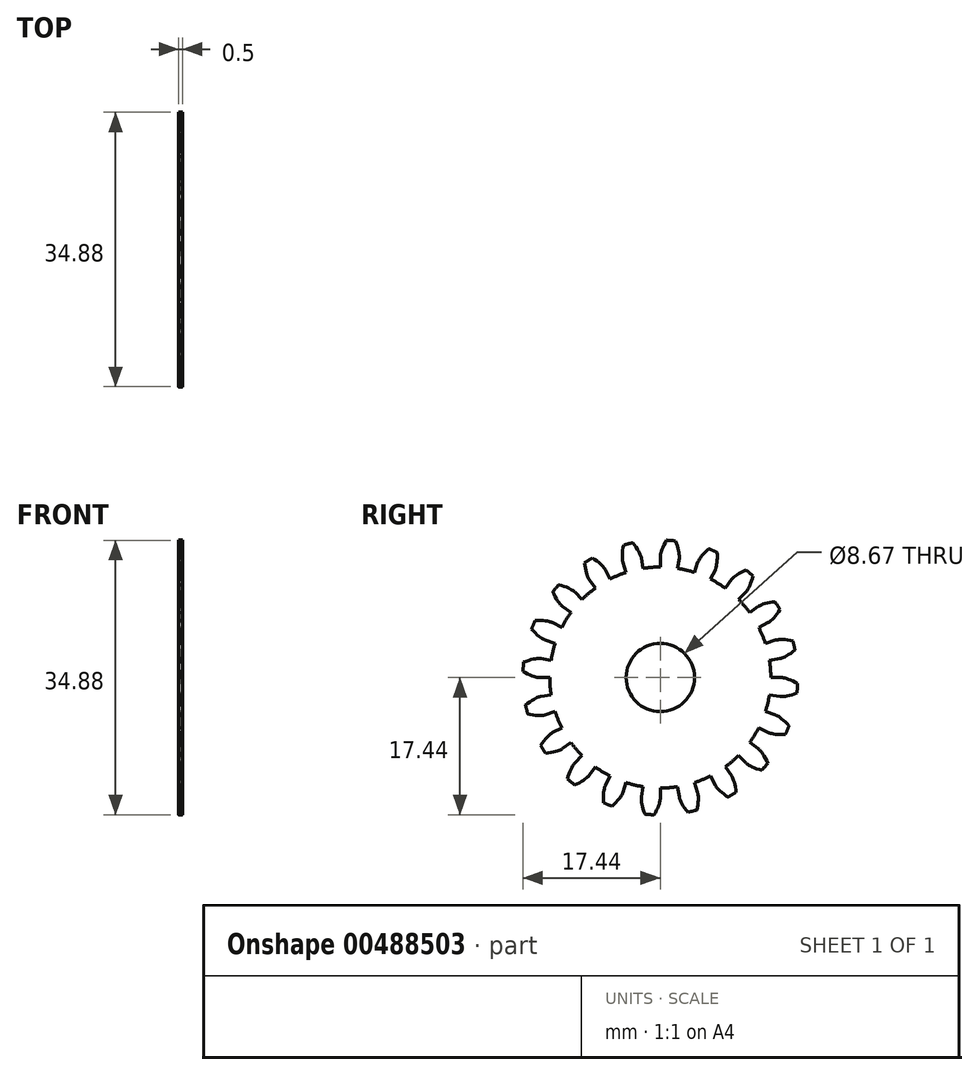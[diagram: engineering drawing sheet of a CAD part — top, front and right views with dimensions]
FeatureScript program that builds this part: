
annotation { "Feature Type Name" : "Feature", "Feature Type Description" : "" }
export const myFeature = defineFeature(function(context is Context, id is Id, definition is map)
    precondition{}
    {
        {
            assignVariable(context, id + "F0", {"name" : "GearThickness", "anyValue" : .5});
        }
        {
            var Q0;
            Q0=qCreatedBy(makeId("Right.planeOp"),FACE);
            var sketch = newSketch(context, id + "F1", { "sketchPlane" : qUnion([Q0])});
            skCircle(sketch, "E0", {"center": v(0, 0) * mm, "radius": 14.04 * mm});
            skCircle(sketch, "E1", {"center": v(0, 0) * mm, "radius": 15.37 * mm, "construction": true});
            skCircle(sketch, "E2", {"center": v(0, 0) * mm, "radius": 15.88 * mm, "construction": true});
            skCircle(sketch, "E3", {"center": v(0, 0) * mm, "radius": 17.46 * mm});
            skLineSegment(sketch, "E4", {"start": v(0, 0) * mm, "end": v(-15.37, 0) * mm, "construction": true});
            skLineSegment(sketch, "E5.1.0", {"start": v(0, 0) * mm, "end": v(-15.35, 0.77) * mm, "construction": true});
            skLineSegment(sketch, "E5.2.0", {"start": v(0, 0) * mm, "end": v(-15.3, 1.53) * mm, "construction": true});
            skLineSegment(sketch, "E5.3.0", {"start": v(0, 0) * mm, "end": v(-15.2, 2.3) * mm, "construction": true});
            skLineSegment(sketch, "E5.4.0", {"start": v(0, 0) * mm, "end": v(-15.06, 3.05) * mm, "construction": true});
            skLineSegment(sketch, "E5.5.0", {"start": v(0, 0) * mm, "end": v(-14.9, 3.8) * mm, "construction": true});
            skLineSegment(sketch, "E5.6.0", {"start": v(0, 0) * mm, "end": v(-14.68, 4.54) * mm, "construction": true});
            skLineSegment(sketch, "E5.7.0", {"start": v(0, 0) * mm, "end": v(-14.44, 5.27) * mm, "construction": true});
            skLineSegment(sketch, "E5.8.0", {"start": v(0, 0) * mm, "end": v(-14.16, 5.99) * mm, "construction": true});
            skLineSegment(sketch, "E5.9.0", {"start": v(0, 0) * mm, "end": v(-13.84, 6.69) * mm, "construction": true});
            skLineSegment(sketch, "E5.10.0", {"start": v(0, 0) * mm, "end": v(-13.49, 7.37) * mm, "construction": true});
            skLineSegment(sketch, "E5.11.0", {"start": v(0, 0) * mm, "end": v(-13.1, 8.03) * mm, "construction": true});
            skLineSegment(sketch, "E5.12.0", {"start": v(0, 0) * mm, "end": v(-12.68, 8.68) * mm, "construction": true});
            skLineSegment(sketch, "E5.13.0", {"start": v(0, 0) * mm, "end": v(-12.24, 9.3) * mm, "construction": true});
            skLineSegment(sketch, "E5.14.0", {"start": v(0, 0) * mm, "end": v(-11.76, 9.9) * mm, "construction": true});
            skLineSegment(sketch, "E5.anchor2", {"start": v(0, 0) * mm, "end": v(-11.76, 9.9) * mm, "construction": true});
            skLineSegment(sketch, "E6", {"start": v(-15.35, 0.77) * mm, "end": v(-15.39, 0) * mm, "construction": true});
            skLineSegment(sketch, "E7", {"start": v(-15.3, 1.53) * mm, "end": v(-15.45, 0) * mm, "construction": true});
            skLineSegment(sketch, "E8", {"start": v(-15.2, 2.3) * mm, "end": v(-15.54, 0.02) * mm, "construction": true});
            skLineSegment(sketch, "E9", {"start": v(-14.9, 3.8) * mm, "end": v(-15.84, 0.08) * mm, "construction": true});
            skLineSegment(sketch, "E10", {"start": v(-14.68, 4.54) * mm, "end": v(-16.05, 0.14) * mm, "construction": true});
            skLineSegment(sketch, "E11", {"start": v(-14.44, 5.27) * mm, "end": v(-16.28, 0.22) * mm, "construction": true});
            skLineSegment(sketch, "E12", {"start": v(-14.16, 5.99) * mm, "end": v(-16.55, 0.32) * mm, "construction": true});
            skLineSegment(sketch, "E13", {"start": v(-13.84, 6.69) * mm, "end": v(-16.85, 0.46) * mm, "construction": true});
            skLineSegment(sketch, "E14", {"start": v(-13.49, 7.37) * mm, "end": v(-17.17, 0.62) * mm, "construction": true});
            skLineSegment(sketch, "E15", {"start": v(-13.1, 8.03) * mm, "end": v(-17.52, 0.83) * mm, "construction": true});
            skLineSegment(sketch, "E16", {"start": v(-15.06, 3.05) * mm, "end": v(-15.67, 0.04) * mm, "construction": true});
            skLineSegment(sketch, "E17", {"start": v(-12.68, 8.68) * mm, "end": v(-17.9, 1.07) * mm, "construction": true});
            skLineSegment(sketch, "E18", {"start": v(-12.24, 9.3) * mm, "end": v(-18.28, 1.35) * mm, "construction": true});
            skLineSegment(sketch, "E19", {"start": v(-11.76, 9.9) * mm, "end": v(-18.69, 1.67) * mm, "construction": true});
            skLineSegment(sketch, "E20", {"start": v(0, 0) * mm, "end": v(-15.32, 1.2) * mm, "construction": true});
            skLineSegment(sketch, "E21", {"start": v(-14.04, 0) * mm, "end": v(-15.37, 0) * mm});
            skLineSegment(sketch, "E22.MirrorCS", {"start": v(-13.87, 2.2) * mm, "end": v(-15.18, 2.4) * mm});
            skLineSegment(sketch, "E23", {"start": v(-15.37, 0) * mm, "end": v(-15.39, 0) * mm});
            skLineSegment(sketch, "E24", {"start": v(-15.39, 0) * mm, "end": v(-15.45, 0) * mm});
            skLineSegment(sketch, "E25", {"start": v(-15.45, 0) * mm, "end": v(-15.54, 0.02) * mm});
            skLineSegment(sketch, "E26", {"start": v(-15.54, 0.02) * mm, "end": v(-15.67, 0.04) * mm});
            skLineSegment(sketch, "E27", {"start": v(-15.67, 0.04) * mm, "end": v(-15.84, 0.08) * mm});
            skLineSegment(sketch, "E28", {"start": v(-15.84, 0.08) * mm, "end": v(-16.05, 0.14) * mm});
            skLineSegment(sketch, "E29", {"start": v(-16.05, 0.14) * mm, "end": v(-16.28, 0.22) * mm});
            skLineSegment(sketch, "E30", {"start": v(-16.28, 0.22) * mm, "end": v(-16.55, 0.32) * mm});
            skLineSegment(sketch, "E31", {"start": v(-16.55, 0.32) * mm, "end": v(-16.85, 0.46) * mm});
            skLineSegment(sketch, "E32", {"start": v(-16.85, 0.46) * mm, "end": v(-17.17, 0.62) * mm});
            skLineSegment(sketch, "E33", {"start": v(-17.17, 0.62) * mm, "end": v(-17.52, 0.83) * mm});
            skLineSegment(sketch, "E34", {"start": v(-17.52, 0.83) * mm, "end": v(-17.9, 1.07) * mm});
            skLineSegment(sketch, "E35", {"start": v(-17.9, 1.07) * mm, "end": v(-18.28, 1.35) * mm});
            skLineSegment(sketch, "E36", {"start": v(-18.28, 1.35) * mm, "end": v(-18.69, 1.67) * mm});
            skLineSegment(sketch, "E37.MirrorCS", {"start": v(-15.18, 2.4) * mm, "end": v(-15.2, 2.4) * mm});
            skLineSegment(sketch, "E38.MirrorCS", {"start": v(-15.2, 2.4) * mm, "end": v(-15.26, 2.41) * mm});
            skLineSegment(sketch, "E39.MirrorCS", {"start": v(-15.26, 2.41) * mm, "end": v(-15.35, 2.41) * mm});
            skLineSegment(sketch, "E40.MirrorCS", {"start": v(-15.35, 2.41) * mm, "end": v(-15.49, 2.41) * mm});
            skLineSegment(sketch, "E41.MirrorCS", {"start": v(-15.66, 2.4) * mm, "end": v(-15.87, 2.37) * mm});
            skLineSegment(sketch, "E42.MirrorCS", {"start": v(-15.87, 2.37) * mm, "end": v(-16.12, 2.33) * mm});
            skLineSegment(sketch, "E43.MirrorCS", {"start": v(-16.12, 2.33) * mm, "end": v(-16.4, 2.27) * mm});
            skLineSegment(sketch, "E44.MirrorCS", {"start": v(-16.4, 2.27) * mm, "end": v(-16.71, 2.18) * mm});
            skLineSegment(sketch, "E45.MirrorCS", {"start": v(-17.06, 2.07) * mm, "end": v(-17.43, 1.92) * mm});
            skLineSegment(sketch, "E46.MirrorCS", {"start": v(-16.71, 2.18) * mm, "end": v(-17.06, 2.07) * mm});
            skLineSegment(sketch, "E47.MirrorCS", {"start": v(-17.43, 1.92) * mm, "end": v(-17.84, 1.74) * mm});
            skLineSegment(sketch, "E48.MirrorCS", {"start": v(-17.84, 1.74) * mm, "end": v(-18.27, 1.53) * mm});
            skLineSegment(sketch, "E49.MirrorCS", {"start": v(-18.27, 1.53) * mm, "end": v(-18.72, 1.27) * mm});
            skLineSegment(sketch, "E50.MirrorCS", {"start": v(-15.49, 2.41) * mm, "end": v(-15.66, 2.4) * mm});
            skLineSegment(sketch, "E51.1.0", {"start": v(-13.35, -4.34) * mm, "end": v(-14.62, -4.75) * mm});
            skLineSegment(sketch, "E51.1.1", {"start": v(-17.18, -3.56) * mm, "end": v(-17.5, -3.85) * mm});
            skLineSegment(sketch, "E51.1.2", {"start": v(-13.87, -2.2) * mm, "end": v(-15.18, -2.4) * mm});
            skLineSegment(sketch, "E51.1.3", {"start": v(-16.86, -3.3) * mm, "end": v(-17.18, -3.56) * mm});
            skLineSegment(sketch, "E51.1.4", {"start": v(-16.52, -4.71) * mm, "end": v(-16.92, -4.63) * mm});
            skLineSegment(sketch, "E51.1.5", {"start": v(-16.92, -4.63) * mm, "end": v(-17.35, -4.51) * mm});
            skLineSegment(sketch, "E51.1.6", {"start": v(-16.57, -3.09) * mm, "end": v(-16.86, -3.3) * mm});
            skLineSegment(sketch, "E51.1.7", {"start": v(-17.85, -4.2) * mm, "end": v(-18.2, -4.58) * mm});
            skLineSegment(sketch, "E51.1.8", {"start": v(-16.3, -2.9) * mm, "end": v(-16.57, -3.09) * mm});
            skLineSegment(sketch, "E51.1.9", {"start": v(-17.8, -4.37) * mm, "end": v(-18.29, -4.18) * mm});
            skLineSegment(sketch, "E51.1.10", {"start": v(-17.5, -3.85) * mm, "end": v(-17.85, -4.2) * mm});
            skLineSegment(sketch, "E51.1.11", {"start": v(-16.16, -4.77) * mm, "end": v(-16.52, -4.71) * mm});
            skLineSegment(sketch, "E51.1.12", {"start": v(-17.35, -4.51) * mm, "end": v(-17.8, -4.37) * mm});
            skLineSegment(sketch, "E51.1.13", {"start": v(-15.63, -2.56) * mm, "end": v(-15.83, -2.65) * mm});
            skLineSegment(sketch, "E51.1.14", {"start": v(-15.83, -2.65) * mm, "end": v(-16.05, -2.76) * mm});
            skLineSegment(sketch, "E51.1.15", {"start": v(-16.05, -2.76) * mm, "end": v(-16.3, -2.9) * mm});
            skLineSegment(sketch, "E51.1.16", {"start": v(-15.55, -4.83) * mm, "end": v(-15.84, -4.8) * mm});
            skLineSegment(sketch, "E51.1.17", {"start": v(-15.3, -4.83) * mm, "end": v(-15.55, -4.83) * mm});
            skLineSegment(sketch, "E51.1.18", {"start": v(-15.84, -4.8) * mm, "end": v(-16.16, -4.77) * mm});
            skLineSegment(sketch, "E51.1.19", {"start": v(-15.47, -2.5) * mm, "end": v(-15.63, -2.56) * mm});
            skLineSegment(sketch, "E51.1.20", {"start": v(-15.35, -2.45) * mm, "end": v(-15.47, -2.5) * mm});
            skLineSegment(sketch, "E51.1.21", {"start": v(-15.1, -4.82) * mm, "end": v(-15.3, -4.83) * mm});
            skLineSegment(sketch, "E51.1.22", {"start": v(-14.92, -4.8) * mm, "end": v(-15.1, -4.82) * mm});
            skLineSegment(sketch, "E51.1.23", {"start": v(-14.7, -4.77) * mm, "end": v(-14.79, -4.79) * mm});
            skLineSegment(sketch, "E51.1.24", {"start": v(-15.18, -2.4) * mm, "end": v(-15.2, -2.4) * mm});
            skLineSegment(sketch, "E51.1.25", {"start": v(-15.2, -2.4) * mm, "end": v(-15.26, -2.42) * mm});
            skLineSegment(sketch, "E51.1.26", {"start": v(-14.79, -4.79) * mm, "end": v(-14.92, -4.8) * mm});
            skLineSegment(sketch, "E51.1.27", {"start": v(-15.26, -2.42) * mm, "end": v(-15.35, -2.45) * mm});
            skLineSegment(sketch, "E51.1.28", {"start": v(-14.64, -4.75) * mm, "end": v(-14.7, -4.77) * mm});
            skLineSegment(sketch, "E51.1.29", {"start": v(-14.62, -4.75) * mm, "end": v(-14.64, -4.75) * mm});
            skLineSegment(sketch, "E51.2.0", {"start": v(-11.36, -8.25) * mm, "end": v(-12.43, -9.03) * mm});
            skLineSegment(sketch, "E51.2.1", {"start": v(-15.24, -8.7) * mm, "end": v(-15.46, -9.07) * mm});
            skLineSegment(sketch, "E51.2.2", {"start": v(-12.5, -6.37) * mm, "end": v(-13.7, -6.98) * mm});
            skLineSegment(sketch, "E51.2.3", {"start": v(-15.02, -8.35) * mm, "end": v(-15.24, -8.7) * mm});
            skLineSegment(sketch, "E51.2.4", {"start": v(-14.26, -9.59) * mm, "end": v(-14.66, -9.63) * mm});
            skLineSegment(sketch, "E51.2.5", {"start": v(-14.66, -9.63) * mm, "end": v(-15.1, -9.65) * mm});
            skLineSegment(sketch, "E51.2.6", {"start": v(-14.8, -8.06) * mm, "end": v(-15.02, -8.35) * mm});
            skLineSegment(sketch, "E51.2.7", {"start": v(-15.68, -9.5) * mm, "end": v(-15.89, -9.97) * mm});
            skLineSegment(sketch, "E51.2.8", {"start": v(-14.6, -7.8) * mm, "end": v(-14.8, -8.06) * mm});
            skLineSegment(sketch, "E51.2.9", {"start": v(-15.58, -9.65) * mm, "end": v(-16.1, -9.63) * mm});
            skLineSegment(sketch, "E51.2.10", {"start": v(-15.46, -9.07) * mm, "end": v(-15.68, -9.5) * mm});
            skLineSegment(sketch, "E51.2.11", {"start": v(-13.9, -9.53) * mm, "end": v(-14.26, -9.59) * mm});
            skLineSegment(sketch, "E51.2.12", {"start": v(-15.1, -9.65) * mm, "end": v(-15.58, -9.65) * mm});
            skLineSegment(sketch, "E51.2.13", {"start": v(-14.08, -7.26) * mm, "end": v(-14.23, -7.4) * mm});
            skLineSegment(sketch, "E51.2.14", {"start": v(-14.23, -7.4) * mm, "end": v(-14.4, -7.59) * mm});
            skLineSegment(sketch, "E51.2.15", {"start": v(-14.4, -7.59) * mm, "end": v(-14.6, -7.8) * mm});
            skLineSegment(sketch, "E51.2.16", {"start": v(-13.3, -9.4) * mm, "end": v(-13.58, -9.47) * mm});
            skLineSegment(sketch, "E51.2.17", {"start": v(-13.06, -9.32) * mm, "end": v(-13.3, -9.4) * mm});
            skLineSegment(sketch, "E51.2.18", {"start": v(-13.58, -9.47) * mm, "end": v(-13.9, -9.53) * mm});
            skLineSegment(sketch, "E51.2.19", {"start": v(-13.95, -7.15) * mm, "end": v(-14.08, -7.26) * mm});
            skLineSegment(sketch, "E51.2.20", {"start": v(-13.84, -7.07) * mm, "end": v(-13.95, -7.15) * mm});
            skLineSegment(sketch, "E51.2.21", {"start": v(-12.86, -9.25) * mm, "end": v(-13.06, -9.32) * mm});
            skLineSegment(sketch, "E51.2.22", {"start": v(-12.7, -9.18) * mm, "end": v(-12.86, -9.25) * mm});
            skLineSegment(sketch, "E51.2.23", {"start": v(-12.5, -9.07) * mm, "end": v(-12.58, -9.12) * mm});
            skLineSegment(sketch, "E51.2.24", {"start": v(-13.7, -6.98) * mm, "end": v(-13.71, -6.99) * mm});
            skLineSegment(sketch, "E51.2.25", {"start": v(-13.71, -6.99) * mm, "end": v(-13.76, -7.02) * mm});
            skLineSegment(sketch, "E51.2.26", {"start": v(-12.58, -9.12) * mm, "end": v(-12.7, -9.18) * mm});
            skLineSegment(sketch, "E51.2.27", {"start": v(-13.76, -7.02) * mm, "end": v(-13.84, -7.07) * mm});
            skLineSegment(sketch, "E51.2.28", {"start": v(-12.45, -9.04) * mm, "end": v(-12.5, -9.07) * mm});
            skLineSegment(sketch, "E51.2.29", {"start": v(-12.43, -9.03) * mm, "end": v(-12.45, -9.04) * mm});
            skLineSegment(sketch, "E51.3.0", {"start": v(-8.25, -11.36) * mm, "end": v(-9.03, -12.43) * mm});
            skLineSegment(sketch, "E51.3.1", {"start": v(-11.8, -12.97) * mm, "end": v(-11.9, -13.4) * mm});
            skLineSegment(sketch, "E51.3.2", {"start": v(-9.93, -9.93) * mm, "end": v(-10.87, -10.87) * mm});
            skLineSegment(sketch, "E51.3.3", {"start": v(-11.7, -12.58) * mm, "end": v(-11.8, -12.97) * mm});
            skLineSegment(sketch, "E51.3.4", {"start": v(-10.6, -13.53) * mm, "end": v(-10.97, -13.69) * mm});
            skLineSegment(sketch, "E51.3.5", {"start": v(-10.97, -13.69) * mm, "end": v(-11.38, -13.85) * mm});
            skLineSegment(sketch, "E51.3.6", {"start": v(-11.59, -12.24) * mm, "end": v(-11.7, -12.58) * mm});
            skLineSegment(sketch, "E51.3.7", {"start": v(-11.97, -13.88) * mm, "end": v(-12.03, -14.4) * mm});
            skLineSegment(sketch, "E51.3.8", {"start": v(-11.47, -11.93) * mm, "end": v(-11.59, -12.24) * mm});
            skLineSegment(sketch, "E51.3.9", {"start": v(-11.84, -14) * mm, "end": v(-12.34, -14.13) * mm});
            skLineSegment(sketch, "E51.3.10", {"start": v(-11.9, -13.4) * mm, "end": v(-11.97, -13.88) * mm});
            skLineSegment(sketch, "E51.3.11", {"start": v(-10.27, -13.36) * mm, "end": v(-10.6, -13.53) * mm});
            skLineSegment(sketch, "E51.3.12", {"start": v(-11.38, -13.85) * mm, "end": v(-11.84, -14) * mm});
            skLineSegment(sketch, "E51.3.13", {"start": v(-11.15, -11.26) * mm, "end": v(-11.25, -11.44) * mm});
            skLineSegment(sketch, "E51.3.14", {"start": v(-11.25, -11.44) * mm, "end": v(-11.36, -11.67) * mm});
            skLineSegment(sketch, "E51.3.15", {"start": v(-11.36, -11.67) * mm, "end": v(-11.47, -11.93) * mm});
            skLineSegment(sketch, "E51.3.16", {"start": v(-9.75, -13.04) * mm, "end": v(-9.99, -13.2) * mm});
            skLineSegment(sketch, "E51.3.17", {"start": v(-9.54, -12.9) * mm, "end": v(-9.75, -13.04) * mm});
            skLineSegment(sketch, "E51.3.18", {"start": v(-9.99, -13.2) * mm, "end": v(-10.27, -13.36) * mm});
            skLineSegment(sketch, "E51.3.19", {"start": v(-11.05, -11.11) * mm, "end": v(-11.15, -11.26) * mm});
            skLineSegment(sketch, "E51.3.20", {"start": v(-10.98, -11) * mm, "end": v(-11.05, -11.11) * mm});
            skLineSegment(sketch, "E51.3.21", {"start": v(-9.38, -12.77) * mm, "end": v(-9.54, -12.9) * mm});
            skLineSegment(sketch, "E51.3.22", {"start": v(-9.25, -12.66) * mm, "end": v(-9.38, -12.77) * mm});
            skLineSegment(sketch, "E51.3.23", {"start": v(-9.08, -12.5) * mm, "end": v(-9.15, -12.56) * mm});
            skLineSegment(sketch, "E51.3.24", {"start": v(-10.87, -10.87) * mm, "end": v(-10.88, -10.88) * mm});
            skLineSegment(sketch, "E51.3.25", {"start": v(-10.88, -10.88) * mm, "end": v(-10.92, -10.93) * mm});
            skLineSegment(sketch, "E51.3.26", {"start": v(-9.15, -12.56) * mm, "end": v(-9.25, -12.66) * mm});
            skLineSegment(sketch, "E51.3.27", {"start": v(-10.92, -10.93) * mm, "end": v(-10.98, -11) * mm});
            skLineSegment(sketch, "E51.3.28", {"start": v(-9.05, -12.45) * mm, "end": v(-9.08, -12.5) * mm});
            skLineSegment(sketch, "E51.3.29", {"start": v(-9.03, -12.43) * mm, "end": v(-9.05, -12.45) * mm});
            skLineSegment(sketch, "E51.4.0", {"start": v(-4.34, -13.35) * mm, "end": v(-4.75, -14.62) * mm});
            skLineSegment(sketch, "E51.4.1", {"start": v(-7.22, -15.99) * mm, "end": v(-7.17, -16.43) * mm});
            skLineSegment(sketch, "E51.4.2", {"start": v(-6.37, -12.5) * mm, "end": v(-6.98, -13.7) * mm});
            skLineSegment(sketch, "E51.4.3", {"start": v(-7.24, -15.58) * mm, "end": v(-7.22, -15.99) * mm});
            skLineSegment(sketch, "E51.4.4", {"start": v(-5.9, -16.14) * mm, "end": v(-6.2, -16.4) * mm});
            skLineSegment(sketch, "E51.4.5", {"start": v(-6.2, -16.4) * mm, "end": v(-6.54, -16.69) * mm});
            skLineSegment(sketch, "E51.4.6", {"start": v(-7.24, -15.22) * mm, "end": v(-7.24, -15.58) * mm});
            skLineSegment(sketch, "E51.4.7", {"start": v(-7.1, -16.9) * mm, "end": v(-7, -17.4) * mm});
            skLineSegment(sketch, "E51.4.8", {"start": v(-7.23, -14.9) * mm, "end": v(-7.24, -15.22) * mm});
            skLineSegment(sketch, "E51.4.9", {"start": v(-6.93, -16.97) * mm, "end": v(-7.37, -17.25) * mm});
            skLineSegment(sketch, "E51.4.10", {"start": v(-7.17, -16.43) * mm, "end": v(-7.1, -16.9) * mm});
            skLineSegment(sketch, "E51.4.11", {"start": v(-5.64, -15.88) * mm, "end": v(-5.9, -16.14) * mm});
            skLineSegment(sketch, "E51.4.12", {"start": v(-6.54, -16.69) * mm, "end": v(-6.93, -16.97) * mm});
            skLineSegment(sketch, "E51.4.13", {"start": v(-7.12, -14.15) * mm, "end": v(-7.16, -14.36) * mm});
            skLineSegment(sketch, "E51.4.14", {"start": v(-7.16, -14.36) * mm, "end": v(-7.2, -14.6) * mm});
            skLineSegment(sketch, "E51.4.15", {"start": v(-7.2, -14.6) * mm, "end": v(-7.23, -14.9) * mm});
            skLineSegment(sketch, "E51.4.16", {"start": v(-5.24, -15.42) * mm, "end": v(-5.42, -15.64) * mm});
            skLineSegment(sketch, "E51.4.17", {"start": v(-5.09, -15.22) * mm, "end": v(-5.24, -15.42) * mm});
            skLineSegment(sketch, "E51.4.18", {"start": v(-5.42, -15.64) * mm, "end": v(-5.64, -15.88) * mm});
            skLineSegment(sketch, "E51.4.19", {"start": v(-7.08, -13.98) * mm, "end": v(-7.12, -14.15) * mm});
            skLineSegment(sketch, "E51.4.20", {"start": v(-7.04, -13.86) * mm, "end": v(-7.08, -13.98) * mm});
            skLineSegment(sketch, "E51.4.21", {"start": v(-4.97, -15.04) * mm, "end": v(-5.09, -15.22) * mm});
            skLineSegment(sketch, "E51.4.22", {"start": v(-4.88, -14.9) * mm, "end": v(-4.97, -15.04) * mm});
            skLineSegment(sketch, "E51.4.23", {"start": v(-4.78, -14.69) * mm, "end": v(-4.82, -14.78) * mm});
            skLineSegment(sketch, "E51.4.24", {"start": v(-6.98, -13.7) * mm, "end": v(-6.99, -13.71) * mm});
            skLineSegment(sketch, "E51.4.25", {"start": v(-6.99, -13.71) * mm, "end": v(-7, -13.76) * mm});
            skLineSegment(sketch, "E51.4.26", {"start": v(-4.82, -14.78) * mm, "end": v(-4.88, -14.9) * mm});
            skLineSegment(sketch, "E51.4.27", {"start": v(-7, -13.76) * mm, "end": v(-7.04, -13.86) * mm});
            skLineSegment(sketch, "E51.4.28", {"start": v(-4.76, -14.64) * mm, "end": v(-4.78, -14.69) * mm});
            skLineSegment(sketch, "E51.4.29", {"start": v(-4.75, -14.62) * mm, "end": v(-4.76, -14.64) * mm});
            skLineSegment(sketch, "E51.5.0", {"start": v(0, -14.04) * mm, "end": v(0, -15.37) * mm});
            skLineSegment(sketch, "E51.5.1", {"start": v(-1.92, -17.43) * mm, "end": v(-1.74, -17.84) * mm});
            skLineSegment(sketch, "E51.5.2", {"start": v(-2.2, -13.87) * mm, "end": v(-2.4, -15.18) * mm});
            skLineSegment(sketch, "E51.5.3", {"start": v(-2.07, -17.06) * mm, "end": v(-1.92, -17.43) * mm});
            skLineSegment(sketch, "E51.5.4", {"start": v(-0.62, -17.17) * mm, "end": v(-0.83, -17.52) * mm});
            skLineSegment(sketch, "E51.5.5", {"start": v(-0.83, -17.52) * mm, "end": v(-1.07, -17.9) * mm});
            skLineSegment(sketch, "E51.5.6", {"start": v(-2.18, -16.71) * mm, "end": v(-2.07, -17.06) * mm});
            skLineSegment(sketch, "E51.5.7", {"start": v(-1.53, -18.27) * mm, "end": v(-1.27, -18.72) * mm});
            skLineSegment(sketch, "E51.5.8", {"start": v(-2.27, -16.4) * mm, "end": v(-2.18, -16.71) * mm});
            skLineSegment(sketch, "E51.5.9", {"start": v(-1.35, -18.28) * mm, "end": v(-1.67, -18.69) * mm});
            skLineSegment(sketch, "E51.5.10", {"start": v(-1.74, -17.84) * mm, "end": v(-1.53, -18.27) * mm});
            skLineSegment(sketch, "E51.5.11", {"start": v(-0.46, -16.85) * mm, "end": v(-0.62, -17.17) * mm});
            skLineSegment(sketch, "E51.5.12", {"start": v(-1.07, -17.9) * mm, "end": v(-1.35, -18.28) * mm});
            skLineSegment(sketch, "E51.5.13", {"start": v(-2.4, -15.66) * mm, "end": v(-2.37, -15.87) * mm});
            skLineSegment(sketch, "E51.5.14", {"start": v(-2.37, -15.87) * mm, "end": v(-2.33, -16.12) * mm});
            skLineSegment(sketch, "E51.5.15", {"start": v(-2.33, -16.12) * mm, "end": v(-2.27, -16.4) * mm});
            skLineSegment(sketch, "E51.5.16", {"start": v(-0.22, -16.28) * mm, "end": v(-0.32, -16.55) * mm});
            skLineSegment(sketch, "E51.5.17", {"start": v(-0.14, -16.05) * mm, "end": v(-0.22, -16.28) * mm});
            skLineSegment(sketch, "E51.5.18", {"start": v(-0.32, -16.55) * mm, "end": v(-0.46, -16.85) * mm});
            skLineSegment(sketch, "E51.5.19", {"start": v(-2.41, -15.49) * mm, "end": v(-2.4, -15.66) * mm});
            skLineSegment(sketch, "E51.5.20", {"start": v(-2.41, -15.35) * mm, "end": v(-2.41, -15.49) * mm});
            skLineSegment(sketch, "E51.5.21", {"start": v(-0.08, -15.84) * mm, "end": v(-0.14, -16.05) * mm});
            skLineSegment(sketch, "E51.5.22", {"start": v(-0.04, -15.67) * mm, "end": v(-0.08, -15.84) * mm});
            skLineSegment(sketch, "E51.5.23", {"start": v(0, -15.45) * mm, "end": v(-0.02, -15.54) * mm});
            skLineSegment(sketch, "E51.5.24", {"start": v(-2.4, -15.18) * mm, "end": v(-2.4, -15.2) * mm});
            skLineSegment(sketch, "E51.5.25", {"start": v(-2.4, -15.2) * mm, "end": v(-2.41, -15.26) * mm});
            skLineSegment(sketch, "E51.5.26", {"start": v(-0.02, -15.54) * mm, "end": v(-0.04, -15.67) * mm});
            skLineSegment(sketch, "E51.5.27", {"start": v(-2.41, -15.26) * mm, "end": v(-2.41, -15.35) * mm});
            skLineSegment(sketch, "E51.5.28", {"start": v(0, -15.39) * mm, "end": v(0, -15.45) * mm});
            skLineSegment(sketch, "E51.5.29", {"start": v(0, -15.37) * mm, "end": v(0, -15.39) * mm});
            skLineSegment(sketch, "E51.6.0", {"start": v(4.34, -13.35) * mm, "end": v(4.75, -14.62) * mm});
            skLineSegment(sketch, "E51.6.1", {"start": v(3.56, -17.18) * mm, "end": v(3.85, -17.5) * mm});
            skLineSegment(sketch, "E51.6.2", {"start": v(2.2, -13.87) * mm, "end": v(2.4, -15.18) * mm});
            skLineSegment(sketch, "E51.6.3", {"start": v(3.3, -16.86) * mm, "end": v(3.56, -17.18) * mm});
            skLineSegment(sketch, "E51.6.4", {"start": v(4.71, -16.52) * mm, "end": v(4.63, -16.92) * mm});
            skLineSegment(sketch, "E51.6.5", {"start": v(4.63, -16.92) * mm, "end": v(4.51, -17.35) * mm});
            skLineSegment(sketch, "E51.6.6", {"start": v(3.09, -16.57) * mm, "end": v(3.3, -16.86) * mm});
            skLineSegment(sketch, "E51.6.7", {"start": v(4.2, -17.85) * mm, "end": v(4.58, -18.2) * mm});
            skLineSegment(sketch, "E51.6.8", {"start": v(2.9, -16.3) * mm, "end": v(3.09, -16.57) * mm});
            skLineSegment(sketch, "E51.6.9", {"start": v(4.37, -17.8) * mm, "end": v(4.18, -18.29) * mm});
            skLineSegment(sketch, "E51.6.10", {"start": v(3.85, -17.5) * mm, "end": v(4.2, -17.85) * mm});
            skLineSegment(sketch, "E51.6.11", {"start": v(4.77, -16.16) * mm, "end": v(4.71, -16.52) * mm});
            skLineSegment(sketch, "E51.6.12", {"start": v(4.51, -17.35) * mm, "end": v(4.37, -17.8) * mm});
            skLineSegment(sketch, "E51.6.13", {"start": v(2.56, -15.63) * mm, "end": v(2.65, -15.83) * mm});
            skLineSegment(sketch, "E51.6.14", {"start": v(2.65, -15.83) * mm, "end": v(2.76, -16.05) * mm});
            skLineSegment(sketch, "E51.6.15", {"start": v(2.76, -16.05) * mm, "end": v(2.9, -16.3) * mm});
            skLineSegment(sketch, "E51.6.16", {"start": v(4.83, -15.55) * mm, "end": v(4.8, -15.84) * mm});
            skLineSegment(sketch, "E51.6.17", {"start": v(4.83, -15.3) * mm, "end": v(4.83, -15.55) * mm});
            skLineSegment(sketch, "E51.6.18", {"start": v(4.8, -15.84) * mm, "end": v(4.77, -16.16) * mm});
            skLineSegment(sketch, "E51.6.19", {"start": v(2.5, -15.47) * mm, "end": v(2.56, -15.63) * mm});
            skLineSegment(sketch, "E51.6.20", {"start": v(2.45, -15.35) * mm, "end": v(2.5, -15.47) * mm});
            skLineSegment(sketch, "E51.6.21", {"start": v(4.82, -15.1) * mm, "end": v(4.83, -15.3) * mm});
            skLineSegment(sketch, "E51.6.22", {"start": v(4.8, -14.92) * mm, "end": v(4.82, -15.1) * mm});
            skLineSegment(sketch, "E51.6.23", {"start": v(4.77, -14.7) * mm, "end": v(4.79, -14.79) * mm});
            skLineSegment(sketch, "E51.6.24", {"start": v(2.4, -15.18) * mm, "end": v(2.4, -15.2) * mm});
            skLineSegment(sketch, "E51.6.25", {"start": v(2.4, -15.2) * mm, "end": v(2.42, -15.26) * mm});
            skLineSegment(sketch, "E51.6.26", {"start": v(4.79, -14.79) * mm, "end": v(4.8, -14.92) * mm});
            skLineSegment(sketch, "E51.6.27", {"start": v(2.42, -15.26) * mm, "end": v(2.45, -15.35) * mm});
            skLineSegment(sketch, "E51.6.28", {"start": v(4.75, -14.64) * mm, "end": v(4.77, -14.7) * mm});
            skLineSegment(sketch, "E51.6.29", {"start": v(4.75, -14.62) * mm, "end": v(4.75, -14.64) * mm});
            skLineSegment(sketch, "E51.7.0", {"start": v(8.25, -11.36) * mm, "end": v(9.03, -12.43) * mm});
            skLineSegment(sketch, "E51.7.1", {"start": v(8.7, -15.24) * mm, "end": v(9.07, -15.46) * mm});
            skLineSegment(sketch, "E51.7.2", {"start": v(6.37, -12.5) * mm, "end": v(6.98, -13.7) * mm});
            skLineSegment(sketch, "E51.7.3", {"start": v(8.35, -15.02) * mm, "end": v(8.7, -15.24) * mm});
            skLineSegment(sketch, "E51.7.4", {"start": v(9.59, -14.26) * mm, "end": v(9.63, -14.66) * mm});
            skLineSegment(sketch, "E51.7.5", {"start": v(9.63, -14.66) * mm, "end": v(9.65, -15.1) * mm});
            skLineSegment(sketch, "E51.7.6", {"start": v(8.06, -14.8) * mm, "end": v(8.35, -15.02) * mm});
            skLineSegment(sketch, "E51.7.7", {"start": v(9.5, -15.68) * mm, "end": v(9.97, -15.89) * mm});
            skLineSegment(sketch, "E51.7.8", {"start": v(7.8, -14.6) * mm, "end": v(8.06, -14.8) * mm});
            skLineSegment(sketch, "E51.7.9", {"start": v(9.65, -15.58) * mm, "end": v(9.63, -16.1) * mm});
            skLineSegment(sketch, "E51.7.10", {"start": v(9.07, -15.46) * mm, "end": v(9.5, -15.68) * mm});
            skLineSegment(sketch, "E51.7.11", {"start": v(9.53, -13.9) * mm, "end": v(9.59, -14.26) * mm});
            skLineSegment(sketch, "E51.7.12", {"start": v(9.65, -15.1) * mm, "end": v(9.65, -15.58) * mm});
            skLineSegment(sketch, "E51.7.13", {"start": v(7.26, -14.08) * mm, "end": v(7.4, -14.23) * mm});
            skLineSegment(sketch, "E51.7.14", {"start": v(7.4, -14.23) * mm, "end": v(7.59, -14.4) * mm});
            skLineSegment(sketch, "E51.7.15", {"start": v(7.59, -14.4) * mm, "end": v(7.8, -14.6) * mm});
            skLineSegment(sketch, "E51.7.16", {"start": v(9.4, -13.3) * mm, "end": v(9.47, -13.58) * mm});
            skLineSegment(sketch, "E51.7.17", {"start": v(9.32, -13.06) * mm, "end": v(9.4, -13.3) * mm});
            skLineSegment(sketch, "E51.7.18", {"start": v(9.47, -13.58) * mm, "end": v(9.53, -13.9) * mm});
            skLineSegment(sketch, "E51.7.19", {"start": v(7.15, -13.95) * mm, "end": v(7.26, -14.08) * mm});
            skLineSegment(sketch, "E51.7.20", {"start": v(7.07, -13.84) * mm, "end": v(7.15, -13.95) * mm});
            skLineSegment(sketch, "E51.7.21", {"start": v(9.25, -12.86) * mm, "end": v(9.32, -13.06) * mm});
            skLineSegment(sketch, "E51.7.22", {"start": v(9.18, -12.7) * mm, "end": v(9.25, -12.86) * mm});
            skLineSegment(sketch, "E51.7.23", {"start": v(9.07, -12.5) * mm, "end": v(9.12, -12.58) * mm});
            skLineSegment(sketch, "E51.7.24", {"start": v(6.98, -13.7) * mm, "end": v(6.99, -13.71) * mm});
            skLineSegment(sketch, "E51.7.25", {"start": v(6.99, -13.71) * mm, "end": v(7.02, -13.76) * mm});
            skLineSegment(sketch, "E51.7.26", {"start": v(9.12, -12.58) * mm, "end": v(9.18, -12.7) * mm});
            skLineSegment(sketch, "E51.7.27", {"start": v(7.02, -13.76) * mm, "end": v(7.07, -13.84) * mm});
            skLineSegment(sketch, "E51.7.28", {"start": v(9.04, -12.45) * mm, "end": v(9.07, -12.5) * mm});
            skLineSegment(sketch, "E51.7.29", {"start": v(9.03, -12.43) * mm, "end": v(9.04, -12.45) * mm});
            skLineSegment(sketch, "E51.8.0", {"start": v(11.36, -8.25) * mm, "end": v(12.43, -9.03) * mm});
            skLineSegment(sketch, "E51.8.1", {"start": v(12.97, -11.8) * mm, "end": v(13.4, -11.9) * mm});
            skLineSegment(sketch, "E51.8.2", {"start": v(9.93, -9.93) * mm, "end": v(10.87, -10.87) * mm});
            skLineSegment(sketch, "E51.8.3", {"start": v(12.58, -11.7) * mm, "end": v(12.97, -11.8) * mm});
            skLineSegment(sketch, "E51.8.4", {"start": v(13.53, -10.6) * mm, "end": v(13.69, -10.97) * mm});
            skLineSegment(sketch, "E51.8.5", {"start": v(13.69, -10.97) * mm, "end": v(13.85, -11.38) * mm});
            skLineSegment(sketch, "E51.8.6", {"start": v(12.24, -11.59) * mm, "end": v(12.58, -11.7) * mm});
            skLineSegment(sketch, "E51.8.7", {"start": v(13.88, -11.97) * mm, "end": v(14.4, -12.03) * mm});
            skLineSegment(sketch, "E51.8.8", {"start": v(11.93, -11.47) * mm, "end": v(12.24, -11.59) * mm});
            skLineSegment(sketch, "E51.8.9", {"start": v(14, -11.84) * mm, "end": v(14.13, -12.34) * mm});
            skLineSegment(sketch, "E51.8.10", {"start": v(13.4, -11.9) * mm, "end": v(13.88, -11.97) * mm});
            skLineSegment(sketch, "E51.8.11", {"start": v(13.36, -10.27) * mm, "end": v(13.53, -10.6) * mm});
            skLineSegment(sketch, "E51.8.12", {"start": v(13.85, -11.38) * mm, "end": v(14, -11.84) * mm});
            skLineSegment(sketch, "E51.8.13", {"start": v(11.26, -11.15) * mm, "end": v(11.44, -11.25) * mm});
            skLineSegment(sketch, "E51.8.14", {"start": v(11.44, -11.25) * mm, "end": v(11.67, -11.36) * mm});
            skLineSegment(sketch, "E51.8.15", {"start": v(11.67, -11.36) * mm, "end": v(11.93, -11.47) * mm});
            skLineSegment(sketch, "E51.8.16", {"start": v(13.04, -9.75) * mm, "end": v(13.2, -9.99) * mm});
            skLineSegment(sketch, "E51.8.17", {"start": v(12.9, -9.54) * mm, "end": v(13.04, -9.75) * mm});
            skLineSegment(sketch, "E51.8.18", {"start": v(13.2, -9.99) * mm, "end": v(13.36, -10.27) * mm});
            skLineSegment(sketch, "E51.8.19", {"start": v(11.11, -11.05) * mm, "end": v(11.26, -11.15) * mm});
            skLineSegment(sketch, "E51.8.20", {"start": v(11, -10.98) * mm, "end": v(11.11, -11.05) * mm});
            skLineSegment(sketch, "E51.8.21", {"start": v(12.77, -9.38) * mm, "end": v(12.9, -9.54) * mm});
            skLineSegment(sketch, "E51.8.22", {"start": v(12.66, -9.25) * mm, "end": v(12.77, -9.38) * mm});
            skLineSegment(sketch, "E51.8.23", {"start": v(12.5, -9.08) * mm, "end": v(12.56, -9.15) * mm});
            skLineSegment(sketch, "E51.8.24", {"start": v(10.87, -10.87) * mm, "end": v(10.88, -10.88) * mm});
            skLineSegment(sketch, "E51.8.25", {"start": v(10.88, -10.88) * mm, "end": v(10.93, -10.92) * mm});
            skLineSegment(sketch, "E51.8.26", {"start": v(12.56, -9.15) * mm, "end": v(12.66, -9.25) * mm});
            skLineSegment(sketch, "E51.8.27", {"start": v(10.93, -10.92) * mm, "end": v(11, -10.98) * mm});
            skLineSegment(sketch, "E51.8.28", {"start": v(12.45, -9.05) * mm, "end": v(12.5, -9.08) * mm});
            skLineSegment(sketch, "E51.8.29", {"start": v(12.43, -9.03) * mm, "end": v(12.45, -9.05) * mm});
            skLineSegment(sketch, "E51.9.0", {"start": v(13.35, -4.34) * mm, "end": v(14.62, -4.75) * mm});
            skLineSegment(sketch, "E51.9.1", {"start": v(15.99, -7.22) * mm, "end": v(16.43, -7.17) * mm});
            skLineSegment(sketch, "E51.9.2", {"start": v(12.5, -6.37) * mm, "end": v(13.7, -6.98) * mm});
            skLineSegment(sketch, "E51.9.3", {"start": v(15.58, -7.24) * mm, "end": v(15.99, -7.22) * mm});
            skLineSegment(sketch, "E51.9.4", {"start": v(16.14, -5.9) * mm, "end": v(16.4, -6.2) * mm});
            skLineSegment(sketch, "E51.9.5", {"start": v(16.4, -6.2) * mm, "end": v(16.69, -6.54) * mm});
            skLineSegment(sketch, "E51.9.6", {"start": v(15.22, -7.24) * mm, "end": v(15.58, -7.24) * mm});
            skLineSegment(sketch, "E51.9.7", {"start": v(16.9, -7.1) * mm, "end": v(17.4, -7) * mm});
            skLineSegment(sketch, "E51.9.8", {"start": v(14.9, -7.23) * mm, "end": v(15.22, -7.24) * mm});
            skLineSegment(sketch, "E51.9.9", {"start": v(16.97, -6.93) * mm, "end": v(17.25, -7.37) * mm});
            skLineSegment(sketch, "E51.9.10", {"start": v(16.43, -7.17) * mm, "end": v(16.9, -7.1) * mm});
            skLineSegment(sketch, "E51.9.11", {"start": v(15.88, -5.64) * mm, "end": v(16.14, -5.9) * mm});
            skLineSegment(sketch, "E51.9.12", {"start": v(16.69, -6.54) * mm, "end": v(16.97, -6.93) * mm});
            skLineSegment(sketch, "E51.9.13", {"start": v(14.15, -7.12) * mm, "end": v(14.36, -7.16) * mm});
            skLineSegment(sketch, "E51.9.14", {"start": v(14.36, -7.16) * mm, "end": v(14.6, -7.2) * mm});
            skLineSegment(sketch, "E51.9.15", {"start": v(14.6, -7.2) * mm, "end": v(14.9, -7.23) * mm});
            skLineSegment(sketch, "E51.9.16", {"start": v(15.42, -5.24) * mm, "end": v(15.64, -5.42) * mm});
            skLineSegment(sketch, "E51.9.17", {"start": v(15.22, -5.09) * mm, "end": v(15.42, -5.24) * mm});
            skLineSegment(sketch, "E51.9.18", {"start": v(15.64, -5.42) * mm, "end": v(15.88, -5.64) * mm});
            skLineSegment(sketch, "E51.9.19", {"start": v(13.98, -7.08) * mm, "end": v(14.15, -7.12) * mm});
            skLineSegment(sketch, "E51.9.20", {"start": v(13.86, -7.04) * mm, "end": v(13.98, -7.08) * mm});
            skLineSegment(sketch, "E51.9.21", {"start": v(15.04, -4.97) * mm, "end": v(15.22, -5.09) * mm});
            skLineSegment(sketch, "E51.9.22", {"start": v(14.9, -4.88) * mm, "end": v(15.04, -4.97) * mm});
            skLineSegment(sketch, "E51.9.23", {"start": v(14.69, -4.78) * mm, "end": v(14.78, -4.82) * mm});
            skLineSegment(sketch, "E51.9.24", {"start": v(13.7, -6.98) * mm, "end": v(13.71, -6.99) * mm});
            skLineSegment(sketch, "E51.9.25", {"start": v(13.71, -6.99) * mm, "end": v(13.76, -7) * mm});
            skLineSegment(sketch, "E51.9.26", {"start": v(14.78, -4.82) * mm, "end": v(14.9, -4.88) * mm});
            skLineSegment(sketch, "E51.9.27", {"start": v(13.76, -7) * mm, "end": v(13.86, -7.04) * mm});
            skLineSegment(sketch, "E51.9.28", {"start": v(14.64, -4.76) * mm, "end": v(14.69, -4.78) * mm});
            skLineSegment(sketch, "E51.9.29", {"start": v(14.62, -4.75) * mm, "end": v(14.64, -4.76) * mm});
            skLineSegment(sketch, "E51.10.0", {"start": v(14.04, 0) * mm, "end": v(15.37, 0) * mm});
            skLineSegment(sketch, "E51.10.1", {"start": v(17.43, -1.92) * mm, "end": v(17.84, -1.74) * mm});
            skLineSegment(sketch, "E51.10.2", {"start": v(13.87, -2.2) * mm, "end": v(15.18, -2.4) * mm});
            skLineSegment(sketch, "E51.10.3", {"start": v(17.06, -2.07) * mm, "end": v(17.43, -1.92) * mm});
            skLineSegment(sketch, "E51.10.4", {"start": v(17.17, -0.62) * mm, "end": v(17.52, -0.83) * mm});
            skLineSegment(sketch, "E51.10.5", {"start": v(17.52, -0.83) * mm, "end": v(17.9, -1.07) * mm});
            skLineSegment(sketch, "E51.10.6", {"start": v(16.71, -2.18) * mm, "end": v(17.06, -2.07) * mm});
            skLineSegment(sketch, "E51.10.7", {"start": v(18.27, -1.53) * mm, "end": v(18.72, -1.27) * mm});
            skLineSegment(sketch, "E51.10.8", {"start": v(16.4, -2.27) * mm, "end": v(16.71, -2.18) * mm});
            skLineSegment(sketch, "E51.10.9", {"start": v(18.28, -1.35) * mm, "end": v(18.69, -1.67) * mm});
            skLineSegment(sketch, "E51.10.10", {"start": v(17.84, -1.74) * mm, "end": v(18.27, -1.53) * mm});
            skLineSegment(sketch, "E51.10.11", {"start": v(16.85, -0.46) * mm, "end": v(17.17, -0.62) * mm});
            skLineSegment(sketch, "E51.10.12", {"start": v(17.9, -1.07) * mm, "end": v(18.28, -1.35) * mm});
            skLineSegment(sketch, "E51.10.13", {"start": v(15.66, -2.4) * mm, "end": v(15.87, -2.37) * mm});
            skLineSegment(sketch, "E51.10.14", {"start": v(15.87, -2.37) * mm, "end": v(16.12, -2.33) * mm});
            skLineSegment(sketch, "E51.10.15", {"start": v(16.12, -2.33) * mm, "end": v(16.4, -2.27) * mm});
            skLineSegment(sketch, "E51.10.16", {"start": v(16.28, -0.22) * mm, "end": v(16.55, -0.32) * mm});
            skLineSegment(sketch, "E51.10.17", {"start": v(16.05, -0.14) * mm, "end": v(16.28, -0.22) * mm});
            skLineSegment(sketch, "E51.10.18", {"start": v(16.55, -0.32) * mm, "end": v(16.85, -0.46) * mm});
            skLineSegment(sketch, "E51.10.19", {"start": v(15.49, -2.41) * mm, "end": v(15.66, -2.4) * mm});
            skLineSegment(sketch, "E51.10.20", {"start": v(15.35, -2.41) * mm, "end": v(15.49, -2.41) * mm});
            skLineSegment(sketch, "E51.10.21", {"start": v(15.84, -0.08) * mm, "end": v(16.05, -0.14) * mm});
            skLineSegment(sketch, "E51.10.22", {"start": v(15.67, -0.04) * mm, "end": v(15.84, -0.08) * mm});
            skLineSegment(sketch, "E51.10.23", {"start": v(15.45, 0) * mm, "end": v(15.54, -0.02) * mm});
            skLineSegment(sketch, "E51.10.24", {"start": v(15.18, -2.4) * mm, "end": v(15.2, -2.4) * mm});
            skLineSegment(sketch, "E51.10.25", {"start": v(15.2, -2.4) * mm, "end": v(15.26, -2.41) * mm});
            skLineSegment(sketch, "E51.10.26", {"start": v(15.54, -0.02) * mm, "end": v(15.67, -0.04) * mm});
            skLineSegment(sketch, "E51.10.27", {"start": v(15.26, -2.41) * mm, "end": v(15.35, -2.41) * mm});
            skLineSegment(sketch, "E51.10.28", {"start": v(15.39, 0) * mm, "end": v(15.45, 0) * mm});
            skLineSegment(sketch, "E51.10.29", {"start": v(15.37, 0) * mm, "end": v(15.39, 0) * mm});
            skLineSegment(sketch, "E51.11.0", {"start": v(13.35, 4.34) * mm, "end": v(14.62, 4.75) * mm});
            skLineSegment(sketch, "E51.11.1", {"start": v(17.18, 3.56) * mm, "end": v(17.5, 3.85) * mm});
            skLineSegment(sketch, "E51.11.2", {"start": v(13.87, 2.2) * mm, "end": v(15.18, 2.4) * mm});
            skLineSegment(sketch, "E51.11.3", {"start": v(16.86, 3.3) * mm, "end": v(17.18, 3.56) * mm});
            skLineSegment(sketch, "E51.11.4", {"start": v(16.52, 4.71) * mm, "end": v(16.92, 4.63) * mm});
            skLineSegment(sketch, "E51.11.5", {"start": v(16.92, 4.63) * mm, "end": v(17.35, 4.51) * mm});
            skLineSegment(sketch, "E51.11.6", {"start": v(16.57, 3.09) * mm, "end": v(16.86, 3.3) * mm});
            skLineSegment(sketch, "E51.11.7", {"start": v(17.85, 4.2) * mm, "end": v(18.2, 4.58) * mm});
            skLineSegment(sketch, "E51.11.8", {"start": v(16.3, 2.9) * mm, "end": v(16.57, 3.09) * mm});
            skLineSegment(sketch, "E51.11.9", {"start": v(17.8, 4.37) * mm, "end": v(18.29, 4.18) * mm});
            skLineSegment(sketch, "E51.11.10", {"start": v(17.5, 3.85) * mm, "end": v(17.85, 4.2) * mm});
            skLineSegment(sketch, "E51.11.11", {"start": v(16.16, 4.77) * mm, "end": v(16.52, 4.71) * mm});
            skLineSegment(sketch, "E51.11.12", {"start": v(17.35, 4.51) * mm, "end": v(17.8, 4.37) * mm});
            skLineSegment(sketch, "E51.11.13", {"start": v(15.63, 2.56) * mm, "end": v(15.83, 2.65) * mm});
            skLineSegment(sketch, "E51.11.14", {"start": v(15.83, 2.65) * mm, "end": v(16.05, 2.76) * mm});
            skLineSegment(sketch, "E51.11.15", {"start": v(16.05, 2.76) * mm, "end": v(16.3, 2.9) * mm});
            skLineSegment(sketch, "E51.11.16", {"start": v(15.55, 4.83) * mm, "end": v(15.84, 4.8) * mm});
            skLineSegment(sketch, "E51.11.17", {"start": v(15.3, 4.83) * mm, "end": v(15.55, 4.83) * mm});
            skLineSegment(sketch, "E51.11.18", {"start": v(15.84, 4.8) * mm, "end": v(16.16, 4.77) * mm});
            skLineSegment(sketch, "E51.11.19", {"start": v(15.47, 2.5) * mm, "end": v(15.63, 2.56) * mm});
            skLineSegment(sketch, "E51.11.20", {"start": v(15.35, 2.45) * mm, "end": v(15.47, 2.5) * mm});
            skLineSegment(sketch, "E51.11.21", {"start": v(15.1, 4.82) * mm, "end": v(15.3, 4.83) * mm});
            skLineSegment(sketch, "E51.11.22", {"start": v(14.92, 4.8) * mm, "end": v(15.1, 4.82) * mm});
            skLineSegment(sketch, "E51.11.23", {"start": v(14.7, 4.77) * mm, "end": v(14.79, 4.79) * mm});
            skLineSegment(sketch, "E51.11.24", {"start": v(15.18, 2.4) * mm, "end": v(15.2, 2.4) * mm});
            skLineSegment(sketch, "E51.11.25", {"start": v(15.2, 2.4) * mm, "end": v(15.26, 2.42) * mm});
            skLineSegment(sketch, "E51.11.26", {"start": v(14.79, 4.79) * mm, "end": v(14.92, 4.8) * mm});
            skLineSegment(sketch, "E51.11.27", {"start": v(15.26, 2.42) * mm, "end": v(15.35, 2.45) * mm});
            skLineSegment(sketch, "E51.11.28", {"start": v(14.64, 4.75) * mm, "end": v(14.7, 4.77) * mm});
            skLineSegment(sketch, "E51.11.29", {"start": v(14.62, 4.75) * mm, "end": v(14.64, 4.75) * mm});
            skLineSegment(sketch, "E51.12.0", {"start": v(11.36, 8.25) * mm, "end": v(12.43, 9.03) * mm});
            skLineSegment(sketch, "E51.12.1", {"start": v(15.24, 8.7) * mm, "end": v(15.46, 9.07) * mm});
            skLineSegment(sketch, "E51.12.2", {"start": v(12.5, 6.37) * mm, "end": v(13.7, 6.98) * mm});
            skLineSegment(sketch, "E51.12.3", {"start": v(15.02, 8.35) * mm, "end": v(15.24, 8.7) * mm});
            skLineSegment(sketch, "E51.12.4", {"start": v(14.26, 9.59) * mm, "end": v(14.66, 9.63) * mm});
            skLineSegment(sketch, "E51.12.5", {"start": v(14.66, 9.63) * mm, "end": v(15.1, 9.65) * mm});
            skLineSegment(sketch, "E51.12.6", {"start": v(14.8, 8.06) * mm, "end": v(15.02, 8.35) * mm});
            skLineSegment(sketch, "E51.12.7", {"start": v(15.68, 9.5) * mm, "end": v(15.89, 9.97) * mm});
            skLineSegment(sketch, "E51.12.8", {"start": v(14.6, 7.8) * mm, "end": v(14.8, 8.06) * mm});
            skLineSegment(sketch, "E51.12.9", {"start": v(15.58, 9.65) * mm, "end": v(16.1, 9.63) * mm});
            skLineSegment(sketch, "E51.12.10", {"start": v(15.46, 9.07) * mm, "end": v(15.68, 9.5) * mm});
            skLineSegment(sketch, "E51.12.11", {"start": v(13.9, 9.53) * mm, "end": v(14.26, 9.59) * mm});
            skLineSegment(sketch, "E51.12.12", {"start": v(15.1, 9.65) * mm, "end": v(15.58, 9.65) * mm});
            skLineSegment(sketch, "E51.12.13", {"start": v(14.08, 7.26) * mm, "end": v(14.23, 7.4) * mm});
            skLineSegment(sketch, "E51.12.14", {"start": v(14.23, 7.4) * mm, "end": v(14.4, 7.59) * mm});
            skLineSegment(sketch, "E51.12.15", {"start": v(14.4, 7.59) * mm, "end": v(14.6, 7.8) * mm});
            skLineSegment(sketch, "E51.12.16", {"start": v(13.3, 9.4) * mm, "end": v(13.58, 9.47) * mm});
            skLineSegment(sketch, "E51.12.17", {"start": v(13.06, 9.32) * mm, "end": v(13.3, 9.4) * mm});
            skLineSegment(sketch, "E51.12.18", {"start": v(13.58, 9.47) * mm, "end": v(13.9, 9.53) * mm});
            skLineSegment(sketch, "E51.12.19", {"start": v(13.95, 7.15) * mm, "end": v(14.08, 7.26) * mm});
            skLineSegment(sketch, "E51.12.20", {"start": v(13.84, 7.07) * mm, "end": v(13.95, 7.15) * mm});
            skLineSegment(sketch, "E51.12.21", {"start": v(12.86, 9.25) * mm, "end": v(13.06, 9.32) * mm});
            skLineSegment(sketch, "E51.12.22", {"start": v(12.7, 9.18) * mm, "end": v(12.86, 9.25) * mm});
            skLineSegment(sketch, "E51.12.23", {"start": v(12.5, 9.07) * mm, "end": v(12.58, 9.12) * mm});
            skLineSegment(sketch, "E51.12.24", {"start": v(13.7, 6.98) * mm, "end": v(13.71, 6.99) * mm});
            skLineSegment(sketch, "E51.12.25", {"start": v(13.71, 6.99) * mm, "end": v(13.76, 7.02) * mm});
            skLineSegment(sketch, "E51.12.26", {"start": v(12.58, 9.12) * mm, "end": v(12.7, 9.18) * mm});
            skLineSegment(sketch, "E51.12.27", {"start": v(13.76, 7.02) * mm, "end": v(13.84, 7.07) * mm});
            skLineSegment(sketch, "E51.12.28", {"start": v(12.45, 9.04) * mm, "end": v(12.5, 9.07) * mm});
            skLineSegment(sketch, "E51.12.29", {"start": v(12.43, 9.03) * mm, "end": v(12.45, 9.04) * mm});
            skLineSegment(sketch, "E51.13.0", {"start": v(8.25, 11.36) * mm, "end": v(9.03, 12.43) * mm});
            skLineSegment(sketch, "E51.13.1", {"start": v(11.8, 12.97) * mm, "end": v(11.9, 13.4) * mm});
            skLineSegment(sketch, "E51.13.2", {"start": v(9.93, 9.93) * mm, "end": v(10.87, 10.87) * mm});
            skLineSegment(sketch, "E51.13.3", {"start": v(11.7, 12.58) * mm, "end": v(11.8, 12.97) * mm});
            skLineSegment(sketch, "E51.13.4", {"start": v(10.6, 13.53) * mm, "end": v(10.97, 13.69) * mm});
            skLineSegment(sketch, "E51.13.5", {"start": v(10.97, 13.69) * mm, "end": v(11.38, 13.85) * mm});
            skLineSegment(sketch, "E51.13.6", {"start": v(11.59, 12.24) * mm, "end": v(11.7, 12.58) * mm});
            skLineSegment(sketch, "E51.13.7", {"start": v(11.97, 13.88) * mm, "end": v(12.03, 14.4) * mm});
            skLineSegment(sketch, "E51.13.8", {"start": v(11.47, 11.93) * mm, "end": v(11.59, 12.24) * mm});
            skLineSegment(sketch, "E51.13.9", {"start": v(11.84, 14) * mm, "end": v(12.34, 14.13) * mm});
            skLineSegment(sketch, "E51.13.10", {"start": v(11.9, 13.4) * mm, "end": v(11.97, 13.88) * mm});
            skLineSegment(sketch, "E51.13.11", {"start": v(10.27, 13.36) * mm, "end": v(10.6, 13.53) * mm});
            skLineSegment(sketch, "E51.13.12", {"start": v(11.38, 13.85) * mm, "end": v(11.84, 14) * mm});
            skLineSegment(sketch, "E51.13.13", {"start": v(11.15, 11.26) * mm, "end": v(11.25, 11.44) * mm});
            skLineSegment(sketch, "E51.13.14", {"start": v(11.25, 11.44) * mm, "end": v(11.36, 11.67) * mm});
            skLineSegment(sketch, "E51.13.15", {"start": v(11.36, 11.67) * mm, "end": v(11.47, 11.93) * mm});
            skLineSegment(sketch, "E51.13.16", {"start": v(9.75, 13.04) * mm, "end": v(9.99, 13.2) * mm});
            skLineSegment(sketch, "E51.13.17", {"start": v(9.54, 12.9) * mm, "end": v(9.75, 13.04) * mm});
            skLineSegment(sketch, "E51.13.18", {"start": v(9.99, 13.2) * mm, "end": v(10.27, 13.36) * mm});
            skLineSegment(sketch, "E51.13.19", {"start": v(11.05, 11.11) * mm, "end": v(11.15, 11.26) * mm});
            skLineSegment(sketch, "E51.13.20", {"start": v(10.98, 11) * mm, "end": v(11.05, 11.11) * mm});
            skLineSegment(sketch, "E51.13.21", {"start": v(9.38, 12.77) * mm, "end": v(9.54, 12.9) * mm});
            skLineSegment(sketch, "E51.13.22", {"start": v(9.25, 12.66) * mm, "end": v(9.38, 12.77) * mm});
            skLineSegment(sketch, "E51.13.23", {"start": v(9.08, 12.5) * mm, "end": v(9.15, 12.56) * mm});
            skLineSegment(sketch, "E51.13.24", {"start": v(10.87, 10.87) * mm, "end": v(10.88, 10.88) * mm});
            skLineSegment(sketch, "E51.13.25", {"start": v(10.88, 10.88) * mm, "end": v(10.92, 10.93) * mm});
            skLineSegment(sketch, "E51.13.26", {"start": v(9.15, 12.56) * mm, "end": v(9.25, 12.66) * mm});
            skLineSegment(sketch, "E51.13.27", {"start": v(10.92, 10.93) * mm, "end": v(10.98, 11) * mm});
            skLineSegment(sketch, "E51.13.28", {"start": v(9.05, 12.45) * mm, "end": v(9.08, 12.5) * mm});
            skLineSegment(sketch, "E51.13.29", {"start": v(9.03, 12.43) * mm, "end": v(9.05, 12.45) * mm});
            skLineSegment(sketch, "E51.14.0", {"start": v(4.34, 13.35) * mm, "end": v(4.75, 14.62) * mm});
            skLineSegment(sketch, "E51.14.1", {"start": v(7.22, 15.99) * mm, "end": v(7.17, 16.43) * mm});
            skLineSegment(sketch, "E51.14.2", {"start": v(6.37, 12.5) * mm, "end": v(6.98, 13.7) * mm});
            skLineSegment(sketch, "E51.14.3", {"start": v(7.24, 15.58) * mm, "end": v(7.22, 15.99) * mm});
            skLineSegment(sketch, "E51.14.4", {"start": v(5.9, 16.14) * mm, "end": v(6.2, 16.4) * mm});
            skLineSegment(sketch, "E51.14.5", {"start": v(6.2, 16.4) * mm, "end": v(6.54, 16.69) * mm});
            skLineSegment(sketch, "E51.14.6", {"start": v(7.24, 15.22) * mm, "end": v(7.24, 15.58) * mm});
            skLineSegment(sketch, "E51.14.7", {"start": v(7.1, 16.9) * mm, "end": v(7, 17.4) * mm});
            skLineSegment(sketch, "E51.14.8", {"start": v(7.23, 14.9) * mm, "end": v(7.24, 15.22) * mm});
            skLineSegment(sketch, "E51.14.9", {"start": v(6.93, 16.97) * mm, "end": v(7.37, 17.25) * mm});
            skLineSegment(sketch, "E51.14.10", {"start": v(7.17, 16.43) * mm, "end": v(7.1, 16.9) * mm});
            skLineSegment(sketch, "E51.14.11", {"start": v(5.64, 15.88) * mm, "end": v(5.9, 16.14) * mm});
            skLineSegment(sketch, "E51.14.12", {"start": v(6.54, 16.69) * mm, "end": v(6.93, 16.97) * mm});
            skLineSegment(sketch, "E51.14.13", {"start": v(7.12, 14.15) * mm, "end": v(7.16, 14.36) * mm});
            skLineSegment(sketch, "E51.14.14", {"start": v(7.16, 14.36) * mm, "end": v(7.2, 14.6) * mm});
            skLineSegment(sketch, "E51.14.15", {"start": v(7.2, 14.6) * mm, "end": v(7.23, 14.9) * mm});
            skLineSegment(sketch, "E51.14.16", {"start": v(5.24, 15.42) * mm, "end": v(5.42, 15.64) * mm});
            skLineSegment(sketch, "E51.14.17", {"start": v(5.09, 15.22) * mm, "end": v(5.24, 15.42) * mm});
            skLineSegment(sketch, "E51.14.18", {"start": v(5.42, 15.64) * mm, "end": v(5.64, 15.88) * mm});
            skLineSegment(sketch, "E51.14.19", {"start": v(7.08, 13.98) * mm, "end": v(7.12, 14.15) * mm});
            skLineSegment(sketch, "E51.14.20", {"start": v(7.04, 13.86) * mm, "end": v(7.08, 13.98) * mm});
            skLineSegment(sketch, "E51.14.21", {"start": v(4.97, 15.04) * mm, "end": v(5.09, 15.22) * mm});
            skLineSegment(sketch, "E51.14.22", {"start": v(4.88, 14.9) * mm, "end": v(4.97, 15.04) * mm});
            skLineSegment(sketch, "E51.14.23", {"start": v(4.78, 14.69) * mm, "end": v(4.82, 14.78) * mm});
            skLineSegment(sketch, "E51.14.24", {"start": v(6.98, 13.7) * mm, "end": v(6.99, 13.71) * mm});
            skLineSegment(sketch, "E51.14.25", {"start": v(6.99, 13.71) * mm, "end": v(7, 13.76) * mm});
            skLineSegment(sketch, "E51.14.26", {"start": v(4.82, 14.78) * mm, "end": v(4.88, 14.9) * mm});
            skLineSegment(sketch, "E51.14.27", {"start": v(7, 13.76) * mm, "end": v(7.04, 13.86) * mm});
            skLineSegment(sketch, "E51.14.28", {"start": v(4.76, 14.64) * mm, "end": v(4.78, 14.69) * mm});
            skLineSegment(sketch, "E51.14.29", {"start": v(4.75, 14.62) * mm, "end": v(4.76, 14.64) * mm});
            skLineSegment(sketch, "E51.15.0", {"start": v(0, 14.04) * mm, "end": v(0, 15.37) * mm});
            skLineSegment(sketch, "E51.15.1", {"start": v(1.92, 17.43) * mm, "end": v(1.74, 17.84) * mm});
            skLineSegment(sketch, "E51.15.2", {"start": v(2.2, 13.87) * mm, "end": v(2.4, 15.18) * mm});
            skLineSegment(sketch, "E51.15.3", {"start": v(2.07, 17.06) * mm, "end": v(1.92, 17.43) * mm});
            skLineSegment(sketch, "E51.15.4", {"start": v(0.62, 17.17) * mm, "end": v(0.83, 17.52) * mm});
            skLineSegment(sketch, "E51.15.5", {"start": v(0.83, 17.52) * mm, "end": v(1.07, 17.9) * mm});
            skLineSegment(sketch, "E51.15.6", {"start": v(2.18, 16.71) * mm, "end": v(2.07, 17.06) * mm});
            skLineSegment(sketch, "E51.15.7", {"start": v(1.53, 18.27) * mm, "end": v(1.27, 18.72) * mm});
            skLineSegment(sketch, "E51.15.8", {"start": v(2.27, 16.4) * mm, "end": v(2.18, 16.71) * mm});
            skLineSegment(sketch, "E51.15.9", {"start": v(1.35, 18.28) * mm, "end": v(1.67, 18.69) * mm});
            skLineSegment(sketch, "E51.15.10", {"start": v(1.74, 17.84) * mm, "end": v(1.53, 18.27) * mm});
            skLineSegment(sketch, "E51.15.11", {"start": v(0.46, 16.85) * mm, "end": v(0.62, 17.17) * mm});
            skLineSegment(sketch, "E51.15.12", {"start": v(1.07, 17.9) * mm, "end": v(1.35, 18.28) * mm});
            skLineSegment(sketch, "E51.15.13", {"start": v(2.4, 15.66) * mm, "end": v(2.37, 15.87) * mm});
            skLineSegment(sketch, "E51.15.14", {"start": v(2.37, 15.87) * mm, "end": v(2.33, 16.12) * mm});
            skLineSegment(sketch, "E51.15.15", {"start": v(2.33, 16.12) * mm, "end": v(2.27, 16.4) * mm});
            skLineSegment(sketch, "E51.15.16", {"start": v(0.22, 16.28) * mm, "end": v(0.32, 16.55) * mm});
            skLineSegment(sketch, "E51.15.17", {"start": v(0.14, 16.05) * mm, "end": v(0.22, 16.28) * mm});
            skLineSegment(sketch, "E51.15.18", {"start": v(0.32, 16.55) * mm, "end": v(0.46, 16.85) * mm});
            skLineSegment(sketch, "E51.15.19", {"start": v(2.41, 15.49) * mm, "end": v(2.4, 15.66) * mm});
            skLineSegment(sketch, "E51.15.20", {"start": v(2.41, 15.35) * mm, "end": v(2.41, 15.49) * mm});
            skLineSegment(sketch, "E51.15.21", {"start": v(0.08, 15.84) * mm, "end": v(0.14, 16.05) * mm});
            skLineSegment(sketch, "E51.15.22", {"start": v(0.04, 15.67) * mm, "end": v(0.08, 15.84) * mm});
            skLineSegment(sketch, "E51.15.23", {"start": v(0, 15.45) * mm, "end": v(0.02, 15.54) * mm});
            skLineSegment(sketch, "E51.15.24", {"start": v(2.4, 15.18) * mm, "end": v(2.4, 15.2) * mm});
            skLineSegment(sketch, "E51.15.25", {"start": v(2.4, 15.2) * mm, "end": v(2.41, 15.26) * mm});
            skLineSegment(sketch, "E51.15.26", {"start": v(0.02, 15.54) * mm, "end": v(0.04, 15.67) * mm});
            skLineSegment(sketch, "E51.15.27", {"start": v(2.41, 15.26) * mm, "end": v(2.41, 15.35) * mm});
            skLineSegment(sketch, "E51.15.28", {"start": v(0, 15.39) * mm, "end": v(0, 15.45) * mm});
            skLineSegment(sketch, "E51.15.29", {"start": v(0, 15.37) * mm, "end": v(0, 15.39) * mm});
            skLineSegment(sketch, "E51.16.0", {"start": v(-4.34, 13.35) * mm, "end": v(-4.75, 14.62) * mm});
            skLineSegment(sketch, "E51.16.1", {"start": v(-3.56, 17.18) * mm, "end": v(-3.85, 17.5) * mm});
            skLineSegment(sketch, "E51.16.2", {"start": v(-2.2, 13.87) * mm, "end": v(-2.4, 15.18) * mm});
            skLineSegment(sketch, "E51.16.3", {"start": v(-3.3, 16.86) * mm, "end": v(-3.56, 17.18) * mm});
            skLineSegment(sketch, "E51.16.4", {"start": v(-4.71, 16.52) * mm, "end": v(-4.63, 16.92) * mm});
            skLineSegment(sketch, "E51.16.5", {"start": v(-4.63, 16.92) * mm, "end": v(-4.51, 17.35) * mm});
            skLineSegment(sketch, "E51.16.6", {"start": v(-3.09, 16.57) * mm, "end": v(-3.3, 16.86) * mm});
            skLineSegment(sketch, "E51.16.7", {"start": v(-4.2, 17.85) * mm, "end": v(-4.58, 18.2) * mm});
            skLineSegment(sketch, "E51.16.8", {"start": v(-2.9, 16.3) * mm, "end": v(-3.09, 16.57) * mm});
            skLineSegment(sketch, "E51.16.9", {"start": v(-4.37, 17.8) * mm, "end": v(-4.18, 18.29) * mm});
            skLineSegment(sketch, "E51.16.10", {"start": v(-3.85, 17.5) * mm, "end": v(-4.2, 17.85) * mm});
            skLineSegment(sketch, "E51.16.11", {"start": v(-4.77, 16.16) * mm, "end": v(-4.71, 16.52) * mm});
            skLineSegment(sketch, "E51.16.12", {"start": v(-4.51, 17.35) * mm, "end": v(-4.37, 17.8) * mm});
            skLineSegment(sketch, "E51.16.13", {"start": v(-2.56, 15.63) * mm, "end": v(-2.65, 15.83) * mm});
            skLineSegment(sketch, "E51.16.14", {"start": v(-2.65, 15.83) * mm, "end": v(-2.76, 16.05) * mm});
            skLineSegment(sketch, "E51.16.15", {"start": v(-2.76, 16.05) * mm, "end": v(-2.9, 16.3) * mm});
            skLineSegment(sketch, "E51.16.16", {"start": v(-4.83, 15.55) * mm, "end": v(-4.8, 15.84) * mm});
            skLineSegment(sketch, "E51.16.17", {"start": v(-4.83, 15.3) * mm, "end": v(-4.83, 15.55) * mm});
            skLineSegment(sketch, "E51.16.18", {"start": v(-4.8, 15.84) * mm, "end": v(-4.77, 16.16) * mm});
            skLineSegment(sketch, "E51.16.19", {"start": v(-2.5, 15.47) * mm, "end": v(-2.56, 15.63) * mm});
            skLineSegment(sketch, "E51.16.20", {"start": v(-2.45, 15.35) * mm, "end": v(-2.5, 15.47) * mm});
            skLineSegment(sketch, "E51.16.21", {"start": v(-4.82, 15.1) * mm, "end": v(-4.83, 15.3) * mm});
            skLineSegment(sketch, "E51.16.22", {"start": v(-4.8, 14.92) * mm, "end": v(-4.82, 15.1) * mm});
            skLineSegment(sketch, "E51.16.23", {"start": v(-4.77, 14.7) * mm, "end": v(-4.79, 14.79) * mm});
            skLineSegment(sketch, "E51.16.24", {"start": v(-2.4, 15.18) * mm, "end": v(-2.4, 15.2) * mm});
            skLineSegment(sketch, "E51.16.25", {"start": v(-2.4, 15.2) * mm, "end": v(-2.42, 15.26) * mm});
            skLineSegment(sketch, "E51.16.26", {"start": v(-4.79, 14.79) * mm, "end": v(-4.8, 14.92) * mm});
            skLineSegment(sketch, "E51.16.27", {"start": v(-2.42, 15.26) * mm, "end": v(-2.45, 15.35) * mm});
            skLineSegment(sketch, "E51.16.28", {"start": v(-4.75, 14.64) * mm, "end": v(-4.77, 14.7) * mm});
            skLineSegment(sketch, "E51.16.29", {"start": v(-4.75, 14.62) * mm, "end": v(-4.75, 14.64) * mm});
            skLineSegment(sketch, "E51.17.0", {"start": v(-8.25, 11.36) * mm, "end": v(-9.03, 12.43) * mm});
            skLineSegment(sketch, "E51.17.1", {"start": v(-8.7, 15.24) * mm, "end": v(-9.07, 15.46) * mm});
            skLineSegment(sketch, "E51.17.2", {"start": v(-6.37, 12.5) * mm, "end": v(-6.98, 13.7) * mm});
            skLineSegment(sketch, "E51.17.3", {"start": v(-8.35, 15.02) * mm, "end": v(-8.7, 15.24) * mm});
            skLineSegment(sketch, "E51.17.4", {"start": v(-9.59, 14.26) * mm, "end": v(-9.63, 14.66) * mm});
            skLineSegment(sketch, "E51.17.5", {"start": v(-9.63, 14.66) * mm, "end": v(-9.65, 15.1) * mm});
            skLineSegment(sketch, "E51.17.6", {"start": v(-8.06, 14.8) * mm, "end": v(-8.35, 15.02) * mm});
            skLineSegment(sketch, "E51.17.7", {"start": v(-9.5, 15.68) * mm, "end": v(-9.97, 15.89) * mm});
            skLineSegment(sketch, "E51.17.8", {"start": v(-7.8, 14.6) * mm, "end": v(-8.06, 14.8) * mm});
            skLineSegment(sketch, "E51.17.9", {"start": v(-9.65, 15.58) * mm, "end": v(-9.63, 16.1) * mm});
            skLineSegment(sketch, "E51.17.10", {"start": v(-9.07, 15.46) * mm, "end": v(-9.5, 15.68) * mm});
            skLineSegment(sketch, "E51.17.11", {"start": v(-9.53, 13.9) * mm, "end": v(-9.59, 14.26) * mm});
            skLineSegment(sketch, "E51.17.12", {"start": v(-9.65, 15.1) * mm, "end": v(-9.65, 15.58) * mm});
            skLineSegment(sketch, "E51.17.13", {"start": v(-7.26, 14.08) * mm, "end": v(-7.4, 14.23) * mm});
            skLineSegment(sketch, "E51.17.14", {"start": v(-7.4, 14.23) * mm, "end": v(-7.59, 14.4) * mm});
            skLineSegment(sketch, "E51.17.15", {"start": v(-7.59, 14.4) * mm, "end": v(-7.8, 14.6) * mm});
            skLineSegment(sketch, "E51.17.16", {"start": v(-9.4, 13.3) * mm, "end": v(-9.47, 13.58) * mm});
            skLineSegment(sketch, "E51.17.17", {"start": v(-9.32, 13.06) * mm, "end": v(-9.4, 13.3) * mm});
            skLineSegment(sketch, "E51.17.18", {"start": v(-9.47, 13.58) * mm, "end": v(-9.53, 13.9) * mm});
            skLineSegment(sketch, "E51.17.19", {"start": v(-7.15, 13.95) * mm, "end": v(-7.26, 14.08) * mm});
            skLineSegment(sketch, "E51.17.20", {"start": v(-7.07, 13.84) * mm, "end": v(-7.15, 13.95) * mm});
            skLineSegment(sketch, "E51.17.21", {"start": v(-9.25, 12.86) * mm, "end": v(-9.32, 13.06) * mm});
            skLineSegment(sketch, "E51.17.22", {"start": v(-9.18, 12.7) * mm, "end": v(-9.25, 12.86) * mm});
            skLineSegment(sketch, "E51.17.23", {"start": v(-9.07, 12.5) * mm, "end": v(-9.12, 12.58) * mm});
            skLineSegment(sketch, "E51.17.24", {"start": v(-6.98, 13.7) * mm, "end": v(-6.99, 13.71) * mm});
            skLineSegment(sketch, "E51.17.25", {"start": v(-6.99, 13.71) * mm, "end": v(-7.02, 13.76) * mm});
            skLineSegment(sketch, "E51.17.26", {"start": v(-9.12, 12.58) * mm, "end": v(-9.18, 12.7) * mm});
            skLineSegment(sketch, "E51.17.27", {"start": v(-7.02, 13.76) * mm, "end": v(-7.07, 13.84) * mm});
            skLineSegment(sketch, "E51.17.28", {"start": v(-9.04, 12.45) * mm, "end": v(-9.07, 12.5) * mm});
            skLineSegment(sketch, "E51.17.29", {"start": v(-9.03, 12.43) * mm, "end": v(-9.04, 12.45) * mm});
            skLineSegment(sketch, "E51.18.0", {"start": v(-11.36, 8.25) * mm, "end": v(-12.43, 9.03) * mm});
            skLineSegment(sketch, "E51.18.1", {"start": v(-12.97, 11.8) * mm, "end": v(-13.4, 11.9) * mm});
            skLineSegment(sketch, "E51.18.2", {"start": v(-9.93, 9.93) * mm, "end": v(-10.87, 10.87) * mm});
            skLineSegment(sketch, "E51.18.3", {"start": v(-12.58, 11.7) * mm, "end": v(-12.97, 11.8) * mm});
            skLineSegment(sketch, "E51.18.4", {"start": v(-13.53, 10.6) * mm, "end": v(-13.69, 10.97) * mm});
            skLineSegment(sketch, "E51.18.5", {"start": v(-13.69, 10.97) * mm, "end": v(-13.85, 11.38) * mm});
            skLineSegment(sketch, "E51.18.6", {"start": v(-12.24, 11.59) * mm, "end": v(-12.58, 11.7) * mm});
            skLineSegment(sketch, "E51.18.7", {"start": v(-13.88, 11.97) * mm, "end": v(-14.4, 12.03) * mm});
            skLineSegment(sketch, "E51.18.8", {"start": v(-11.93, 11.47) * mm, "end": v(-12.24, 11.59) * mm});
            skLineSegment(sketch, "E51.18.9", {"start": v(-14, 11.84) * mm, "end": v(-14.13, 12.34) * mm});
            skLineSegment(sketch, "E51.18.10", {"start": v(-13.4, 11.9) * mm, "end": v(-13.88, 11.97) * mm});
            skLineSegment(sketch, "E51.18.11", {"start": v(-13.36, 10.27) * mm, "end": v(-13.53, 10.6) * mm});
            skLineSegment(sketch, "E51.18.12", {"start": v(-13.85, 11.38) * mm, "end": v(-14, 11.84) * mm});
            skLineSegment(sketch, "E51.18.13", {"start": v(-11.26, 11.15) * mm, "end": v(-11.44, 11.25) * mm});
            skLineSegment(sketch, "E51.18.14", {"start": v(-11.44, 11.25) * mm, "end": v(-11.67, 11.36) * mm});
            skLineSegment(sketch, "E51.18.15", {"start": v(-11.67, 11.36) * mm, "end": v(-11.93, 11.47) * mm});
            skLineSegment(sketch, "E51.18.16", {"start": v(-13.04, 9.75) * mm, "end": v(-13.2, 9.99) * mm});
            skLineSegment(sketch, "E51.18.17", {"start": v(-12.9, 9.54) * mm, "end": v(-13.04, 9.75) * mm});
            skLineSegment(sketch, "E51.18.18", {"start": v(-13.2, 9.99) * mm, "end": v(-13.36, 10.27) * mm});
            skLineSegment(sketch, "E51.18.19", {"start": v(-11.11, 11.05) * mm, "end": v(-11.26, 11.15) * mm});
            skLineSegment(sketch, "E51.18.20", {"start": v(-11, 10.98) * mm, "end": v(-11.11, 11.05) * mm});
            skLineSegment(sketch, "E51.18.21", {"start": v(-12.77, 9.38) * mm, "end": v(-12.9, 9.54) * mm});
            skLineSegment(sketch, "E51.18.22", {"start": v(-12.66, 9.25) * mm, "end": v(-12.77, 9.38) * mm});
            skLineSegment(sketch, "E51.18.23", {"start": v(-12.5, 9.08) * mm, "end": v(-12.56, 9.15) * mm});
            skLineSegment(sketch, "E51.18.24", {"start": v(-10.87, 10.87) * mm, "end": v(-10.88, 10.88) * mm});
            skLineSegment(sketch, "E51.18.25", {"start": v(-10.88, 10.88) * mm, "end": v(-10.93, 10.92) * mm});
            skLineSegment(sketch, "E51.18.26", {"start": v(-12.56, 9.15) * mm, "end": v(-12.66, 9.25) * mm});
            skLineSegment(sketch, "E51.18.27", {"start": v(-10.93, 10.92) * mm, "end": v(-11, 10.98) * mm});
            skLineSegment(sketch, "E51.18.28", {"start": v(-12.45, 9.05) * mm, "end": v(-12.5, 9.08) * mm});
            skLineSegment(sketch, "E51.18.29", {"start": v(-12.43, 9.03) * mm, "end": v(-12.45, 9.05) * mm});
            skLineSegment(sketch, "E51.19.0", {"start": v(-13.35, 4.34) * mm, "end": v(-14.62, 4.75) * mm});
            skLineSegment(sketch, "E51.19.1", {"start": v(-15.99, 7.22) * mm, "end": v(-16.43, 7.17) * mm});
            skLineSegment(sketch, "E51.19.2", {"start": v(-12.5, 6.37) * mm, "end": v(-13.7, 6.98) * mm});
            skLineSegment(sketch, "E51.19.3", {"start": v(-15.58, 7.24) * mm, "end": v(-15.99, 7.22) * mm});
            skLineSegment(sketch, "E51.19.4", {"start": v(-16.14, 5.9) * mm, "end": v(-16.4, 6.2) * mm});
            skLineSegment(sketch, "E51.19.5", {"start": v(-16.4, 6.2) * mm, "end": v(-16.69, 6.54) * mm});
            skLineSegment(sketch, "E51.19.6", {"start": v(-15.22, 7.24) * mm, "end": v(-15.58, 7.24) * mm});
            skLineSegment(sketch, "E51.19.7", {"start": v(-16.9, 7.1) * mm, "end": v(-17.4, 7) * mm});
            skLineSegment(sketch, "E51.19.8", {"start": v(-14.9, 7.23) * mm, "end": v(-15.22, 7.24) * mm});
            skLineSegment(sketch, "E51.19.9", {"start": v(-16.97, 6.93) * mm, "end": v(-17.25, 7.37) * mm});
            skLineSegment(sketch, "E51.19.10", {"start": v(-16.43, 7.17) * mm, "end": v(-16.9, 7.1) * mm});
            skLineSegment(sketch, "E51.19.11", {"start": v(-15.88, 5.64) * mm, "end": v(-16.14, 5.9) * mm});
            skLineSegment(sketch, "E51.19.12", {"start": v(-16.69, 6.54) * mm, "end": v(-16.97, 6.93) * mm});
            skLineSegment(sketch, "E51.19.13", {"start": v(-14.15, 7.12) * mm, "end": v(-14.36, 7.16) * mm});
            skLineSegment(sketch, "E51.19.14", {"start": v(-14.36, 7.16) * mm, "end": v(-14.6, 7.2) * mm});
            skLineSegment(sketch, "E51.19.15", {"start": v(-14.6, 7.2) * mm, "end": v(-14.9, 7.23) * mm});
            skLineSegment(sketch, "E51.19.16", {"start": v(-15.42, 5.24) * mm, "end": v(-15.64, 5.42) * mm});
            skLineSegment(sketch, "E51.19.17", {"start": v(-15.22, 5.09) * mm, "end": v(-15.42, 5.24) * mm});
            skLineSegment(sketch, "E51.19.18", {"start": v(-15.64, 5.42) * mm, "end": v(-15.88, 5.64) * mm});
            skLineSegment(sketch, "E51.19.19", {"start": v(-13.98, 7.08) * mm, "end": v(-14.15, 7.12) * mm});
            skLineSegment(sketch, "E51.19.20", {"start": v(-13.86, 7.04) * mm, "end": v(-13.98, 7.08) * mm});
            skLineSegment(sketch, "E51.19.21", {"start": v(-15.04, 4.97) * mm, "end": v(-15.22, 5.09) * mm});
            skLineSegment(sketch, "E51.19.22", {"start": v(-14.9, 4.88) * mm, "end": v(-15.04, 4.97) * mm});
            skLineSegment(sketch, "E51.19.23", {"start": v(-14.69, 4.78) * mm, "end": v(-14.78, 4.82) * mm});
            skLineSegment(sketch, "E51.19.24", {"start": v(-13.7, 6.98) * mm, "end": v(-13.71, 6.99) * mm});
            skLineSegment(sketch, "E51.19.25", {"start": v(-13.71, 6.99) * mm, "end": v(-13.76, 7) * mm});
            skLineSegment(sketch, "E51.19.26", {"start": v(-14.78, 4.82) * mm, "end": v(-14.9, 4.88) * mm});
            skLineSegment(sketch, "E51.19.27", {"start": v(-13.76, 7) * mm, "end": v(-13.86, 7.04) * mm});
            skLineSegment(sketch, "E51.19.28", {"start": v(-14.64, 4.76) * mm, "end": v(-14.69, 4.78) * mm});
            skLineSegment(sketch, "E51.19.29", {"start": v(-14.62, 4.75) * mm, "end": v(-14.64, 4.76) * mm});
            skSolve(sketch);
        }
        {
            var Q0;
            {var subQ0=sQuery(id+"F1.wireOp",EDGE,"E0");var subQ27=makeQuery(id+"F1.imprint","INTERSECT",VERTEX,{"derivedFrom":[subQ0,sQuery(id+"F1.wireOp",EDGE,"E51.10.0")]});Q0=makeQuery(id+"F1.imprint","IMPRINT",FACE,{"disambiguationData":[TD([[makeQuery(id+"F1.imprint","IMPRINT",EDGE,{"disambiguationData":[TD([[subQ27,-1.0]])],"derivedFrom":subQ0}),1.0]])]});}
            var Q1;
            {var subQ0=sQuery(id+"F1.wireOp",EDGE,"E51.1.0");Q1=makeQuery(id+"F1.imprint","IMPRINT",FACE,{"disambiguationData":[TD([[makeQuery(id+"F1.imprint","IMPRINT",EDGE,{"derivedFrom":subQ0}),-1.0]])]});}
            var Q2;
            {var subQ7=sQuery(id+"F1.wireOp",EDGE,"E51.2.0");Q2=makeQuery(id+"F1.imprint","IMPRINT",FACE,{"disambiguationData":[TD([[makeQuery(id+"F1.imprint","IMPRINT",EDGE,{"derivedFrom":subQ7}),-1.0]])]});}
            var Q3;
            {var subQ8=sQuery(id+"F1.wireOp",EDGE,"E51.3.0");Q3=makeQuery(id+"F1.imprint","IMPRINT",FACE,{"disambiguationData":[TD([[makeQuery(id+"F1.imprint","IMPRINT",EDGE,{"derivedFrom":subQ8}),-1.0]])]});}
            var Q4;
            {var subQ2=sQuery(id+"F1.wireOp",EDGE,"E51.4.0");Q4=makeQuery(id+"F1.imprint","IMPRINT",FACE,{"disambiguationData":[TD([[makeQuery(id+"F1.imprint","IMPRINT",EDGE,{"derivedFrom":subQ2}),-1.0]])]});}
            var Q5;
            {var subQ8=sQuery(id+"F1.wireOp",EDGE,"E51.5.0");Q5=makeQuery(id+"F1.imprint","IMPRINT",FACE,{"disambiguationData":[TD([[makeQuery(id+"F1.imprint","IMPRINT",EDGE,{"derivedFrom":subQ8}),-1.0]])]});}
            var Q6;
            {var subQ3=sQuery(id+"F1.wireOp",EDGE,"E51.6.0");Q6=makeQuery(id+"F1.imprint","IMPRINT",FACE,{"disambiguationData":[TD([[makeQuery(id+"F1.imprint","IMPRINT",EDGE,{"derivedFrom":subQ3}),-1.0]])]});}
            var Q7;
            {var subQ0=sQuery(id+"F1.wireOp",EDGE,"E51.7.0");Q7=makeQuery(id+"F1.imprint","IMPRINT",FACE,{"disambiguationData":[TD([[makeQuery(id+"F1.imprint","IMPRINT",EDGE,{"derivedFrom":subQ0}),-1.0]])]});}
            var Q8;
            {var subQ5=sQuery(id+"F1.wireOp",EDGE,"E51.8.0");Q8=makeQuery(id+"F1.imprint","IMPRINT",FACE,{"disambiguationData":[TD([[makeQuery(id+"F1.imprint","IMPRINT",EDGE,{"derivedFrom":subQ5}),-1.0]])]});}
            var Q9;
            {var subQ1=sQuery(id+"F1.wireOp",EDGE,"E51.9.0");Q9=makeQuery(id+"F1.imprint","IMPRINT",FACE,{"disambiguationData":[TD([[makeQuery(id+"F1.imprint","IMPRINT",EDGE,{"derivedFrom":subQ1}),-1.0]])]});}
            var Q10;
            {var subQ5=sQuery(id+"F1.wireOp",EDGE,"E51.10.0");Q10=makeQuery(id+"F1.imprint","IMPRINT",FACE,{"disambiguationData":[TD([[makeQuery(id+"F1.imprint","IMPRINT",EDGE,{"derivedFrom":subQ5}),-1.0]])]});}
            var Q11;
            {var subQ8=sQuery(id+"F1.wireOp",EDGE,"E51.11.0");Q11=makeQuery(id+"F1.imprint","IMPRINT",FACE,{"disambiguationData":[TD([[makeQuery(id+"F1.imprint","IMPRINT",EDGE,{"derivedFrom":subQ8}),-1.0]])]});}
            var Q12;
            {var subQ2=sQuery(id+"F1.wireOp",EDGE,"E51.12.0");Q12=makeQuery(id+"F1.imprint","IMPRINT",FACE,{"disambiguationData":[TD([[makeQuery(id+"F1.imprint","IMPRINT",EDGE,{"derivedFrom":subQ2}),-1.0]])]});}
            var Q13;
            {var subQ3=sQuery(id+"F1.wireOp",EDGE,"E51.13.0");Q13=makeQuery(id+"F1.imprint","IMPRINT",FACE,{"disambiguationData":[TD([[makeQuery(id+"F1.imprint","IMPRINT",EDGE,{"derivedFrom":subQ3}),-1.0]])]});}
            var Q14;
            {var subQ0=sQuery(id+"F1.wireOp",EDGE,"E51.14.0");Q14=makeQuery(id+"F1.imprint","IMPRINT",FACE,{"disambiguationData":[TD([[makeQuery(id+"F1.imprint","IMPRINT",EDGE,{"derivedFrom":subQ0}),-1.0]])]});}
            var Q15;
            {var subQ6=sQuery(id+"F1.wireOp",EDGE,"E51.15.0");Q15=makeQuery(id+"F1.imprint","IMPRINT",FACE,{"disambiguationData":[TD([[makeQuery(id+"F1.imprint","IMPRINT",EDGE,{"derivedFrom":subQ6}),-1.0]])]});}
            var Q16;
            {var subQ5=sQuery(id+"F1.wireOp",EDGE,"E51.16.0");Q16=makeQuery(id+"F1.imprint","IMPRINT",FACE,{"disambiguationData":[TD([[makeQuery(id+"F1.imprint","IMPRINT",EDGE,{"derivedFrom":subQ5}),-1.0]])]});}
            var Q17;
            {var subQ7=sQuery(id+"F1.wireOp",EDGE,"E51.17.0");Q17=makeQuery(id+"F1.imprint","IMPRINT",FACE,{"disambiguationData":[TD([[makeQuery(id+"F1.imprint","IMPRINT",EDGE,{"derivedFrom":subQ7}),-1.0]])]});}
            var Q18;
            {var subQ5=sQuery(id+"F1.wireOp",EDGE,"E51.18.0");Q18=makeQuery(id+"F1.imprint","IMPRINT",FACE,{"disambiguationData":[TD([[makeQuery(id+"F1.imprint","IMPRINT",EDGE,{"derivedFrom":subQ5}),-1.0]])]});}
            var Q19;
            {var subQ8=sQuery(id+"F1.wireOp",EDGE,"E51.19.0");Q19=makeQuery(id+"F1.imprint","IMPRINT",FACE,{"disambiguationData":[TD([[makeQuery(id+"F1.imprint","IMPRINT",EDGE,{"derivedFrom":subQ8}),-1.0]])]});}
            var Q20;
            {var subQ8=sQuery(id+"F1.wireOp",EDGE,"E21");Q20=makeQuery(id+"F1.imprint","IMPRINT",FACE,{"disambiguationData":[TD([[makeQuery(id+"F1.imprint","IMPRINT",EDGE,{"derivedFrom":subQ8}),-1.0]])]});}
            extrude(context, id + "F2", {"entities" : qUnion([Q0, Q1, Q2, Q3, Q4, Q5, Q6, Q7, Q8, Q9, Q10, Q11, Q12, Q13, Q14, Q15, Q16, Q17, Q18, Q19, Q20]), "depth" : (getVariable(context, 'GearThickness')) * mm});
        }
        {
            var Q0;
            Q0=qCreatedBy(makeId("Right.planeOp"),FACE);
            var sketch = newSketch(context, id + "F3", { "sketchPlane" : qUnion([Q0])});
            skCircle(sketch, "E52", {"center": v(0, 0) * mm, "radius": 4.34 * mm});
            skSolve(sketch);
        }
        {
            var Q0;
            Q0=makeQuery(id+"F3.imprint","IMPRINT",FACE,{"disambiguationData":[TD([[makeQuery(id+"F3.imprint","IMPRINT",EDGE,{"derivedFrom":sQuery(id+"F3.wireOp",EDGE,"E52")}),1.0]])]});
            extrude(context, id + "F4", {"entities" : qUnion([Q0]), "operationType" : NewBodyOperationType.REMOVE, "endBound" : BoundingType.THROUGH_ALL, "depth" : 25.4 * mm});
        }
    });
